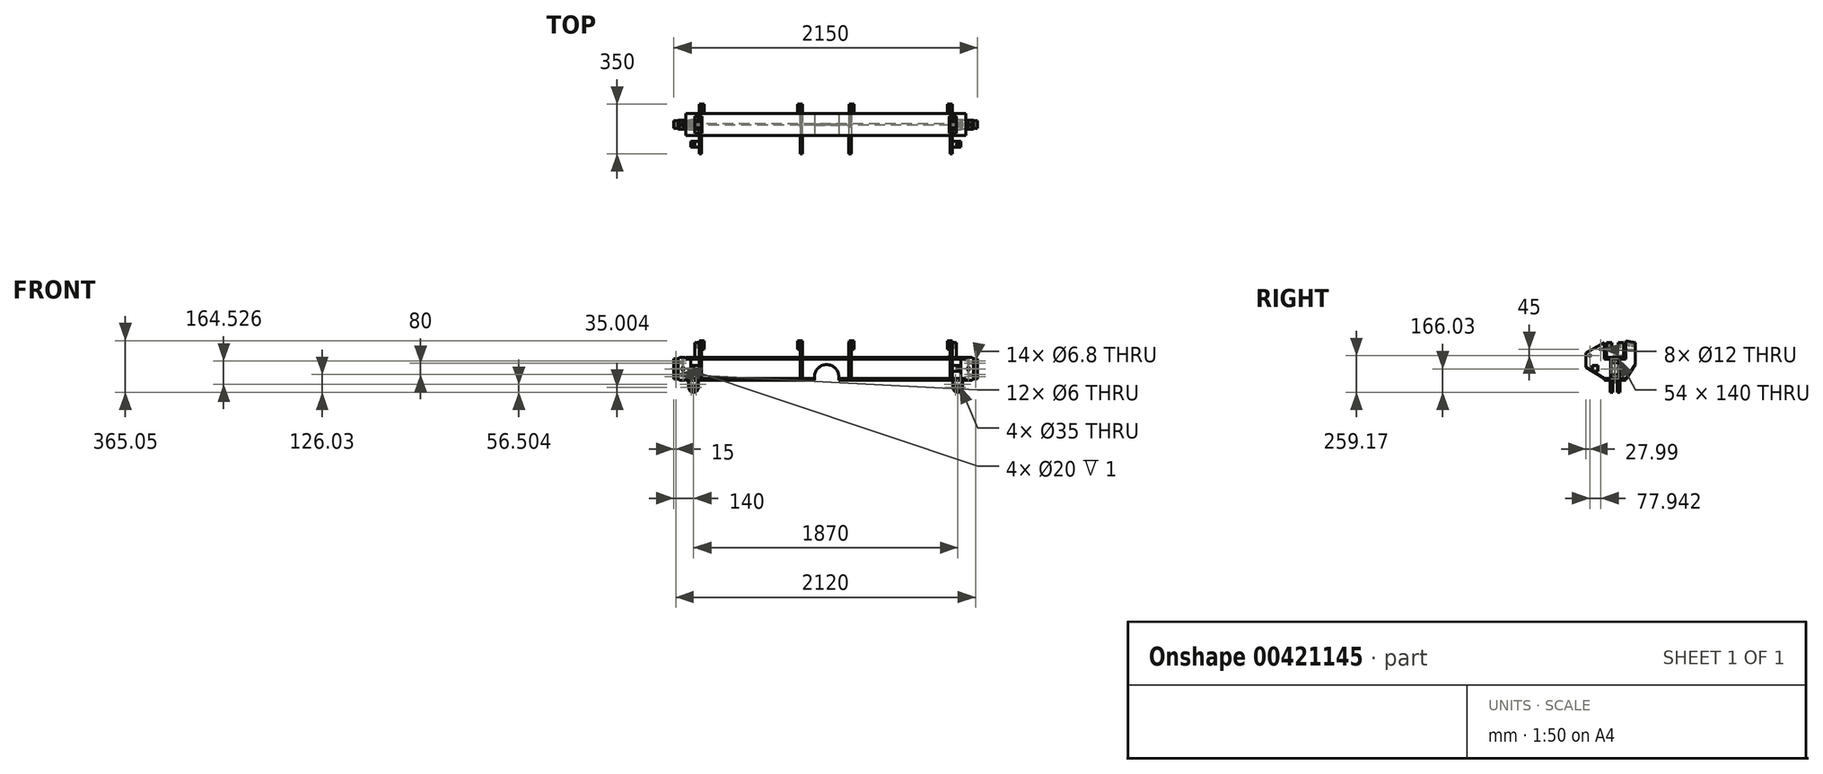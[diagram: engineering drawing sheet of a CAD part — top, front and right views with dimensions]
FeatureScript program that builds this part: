
annotation { "Feature Type Name" : "Feature", "Feature Type Description" : "" }
export const myFeature = defineFeature(function(context is Context, id is Id, definition is map)
    precondition{}
    {
        {
            var Q0;
            Q0=qCreatedBy(makeId("Right.planeOp"),FACE);
            var sketch = newSketch(context, id + "F0", { "sketchPlane" : qUnion([Q0])});
            skLineSegment(sketch, "E0.bottom", {"start": v(-77.22, 81.03) * mm, "end": v(77.22, 81.03) * mm});
            skLineSegment(sketch, "E0.top", {"start": v(-77.22, -81.03) * mm, "end": v(77.22, -81.03) * mm});
            skLineSegment(sketch, "E0.left", {"start": v(-77.22, 81.03) * mm, "end": v(-77.22, 69.47) * mm});
            skLineSegment(sketch, "E0.right", {"start": v(77.22, 81.03) * mm, "end": v(77.22, 69.47) * mm});
            skPoint(sketch, "E0.middle", {"position": v(0, 0) * mm});
            skLineSegment(sketch, "E1", {"start": v(0, 87.3) * mm, "end": v(0, -92.44) * mm, "construction": true});
            skLineSegment(sketch, "E2.0", {"start": v(-77.22, 69.47) * mm, "end": v(-16.76, 69.47) * mm});
            skLineSegment(sketch, "E3.0", {"start": v(-77.22, -69.47) * mm, "end": v(-16.76, -69.47) * mm});
            skLineSegment(sketch, "E4.0", {"start": v(-4.06, 56.77) * mm, "end": v(-4.06, -56.77) * mm});
            skLineSegment(sketch, "E5.0", {"start": v(4.06, 56.77) * mm, "end": v(4.06, -56.77) * mm});
            skLineSegment(sketch, "E6.trimOffspring", {"start": v(16.76, -69.47) * mm, "end": v(77.22, -69.47) * mm});
            skLineSegment(sketch, "E7.trimOffspring", {"start": v(16.76, 69.47) * mm, "end": v(77.22, 69.47) * mm});
            skLineSegment(sketch, "E8.trimOffspring", {"start": v(-77.22, -69.47) * mm, "end": v(-77.22, -81.03) * mm});
            skLineSegment(sketch, "E9.trimOffspring", {"start": v(77.22, -69.47) * mm, "end": v(77.22, -81.03) * mm});
            skPoint(sketch, "E10.visualSharp", {"position": v(-4.06, 69.47) * mm});
            skArc(sketch, "E10.filletArc", {"start": v(-4.06, 56.77) * mm, "mid": v(-7.78, 65.75) * mm, "end": v(-16.76, 69.47) * mm});
            skPoint(sketch, "E11.visualSharp", {"position": v(4.06, 69.47) * mm});
            skArc(sketch, "E11.filletArc", {"start": v(16.76, 69.47) * mm, "mid": v(7.78, 65.75) * mm, "end": v(4.06, 56.77) * mm});
            skPoint(sketch, "E12.visualSharp", {"position": v(4.06, -69.47) * mm});
            skArc(sketch, "E12.filletArc", {"start": v(4.06, -56.77) * mm, "mid": v(7.78, -65.75) * mm, "end": v(16.76, -69.47) * mm});
            skPoint(sketch, "E13.visualSharp", {"position": v(-4.06, -69.47) * mm});
            skArc(sketch, "E13.filletArc", {"start": v(-16.76, -69.47) * mm, "mid": v(-7.78, -65.75) * mm, "end": v(-4.06, -56.77) * mm});
            skSolve(sketch);
        }
        {
            var Q0;
            Q0=qSketchRegion(id+"F0",true);
            extrude(context, id + "F1", {"entities" : qUnion([Q0]), "endBound" : BoundingType.SYMMETRIC, "depth" : 1980 * mm});
        }
        {
            var Q0;
            Q0=makeQuery(id+"F1.opExtrude","SWEPT_FACE",FACE,{"disambiguationData":[OSD([sQuery(id+"F0.wireOp",EDGE,"E4.0")])]});
            var sketch = newSketch(context, id + "F2", { "sketchPlane" : qUnion([Q0])});
            skLineSegment(sketch, "E14", {"start": v(0, 173.84) * mm, "end": v(0, -192.2) * mm, "construction": true});
            skLineSegment(sketch, "E15.0", {"start": v(-990, 69.47) * mm, "end": v(-990, -69.47) * mm, "construction": true});
            skLineSegment(sketch, "E16.0", {"start": v(990, 69.47) * mm, "end": v(-990, 69.47) * mm, "construction": true});
            skLineSegment(sketch, "E17.0", {"start": v(990, -69.47) * mm, "end": v(-990, -69.47) * mm, "construction": true});
            skPoint(sketch, "E18.orphan", {"position": v(-990, 56.77) * mm});
            skPoint(sketch, "E19.orphan", {"position": v(-990, -56.77) * mm});
            skLineSegment(sketch, "E20.bottom", {"start": v(-990, 69.47) * mm, "end": v(-955, 69.47) * mm});
            skLineSegment(sketch, "E20.top", {"start": v(-990, -69.47) * mm, "end": v(-955, -69.47) * mm});
            skLineSegment(sketch, "E20.left", {"start": v(-990, 69.47) * mm, "end": v(-990, -69.47) * mm});
            skLineSegment(sketch, "E20.right", {"start": v(-955, 69.47) * mm, "end": v(-955, -69.47) * mm});
            skLineSegment(sketch, "E21.MirrorCS", {"start": v(990, -69.47) * mm, "end": v(955, -69.47) * mm});
            skLineSegment(sketch, "E22.MirrorCS", {"start": v(990, 69.47) * mm, "end": v(955, 69.47) * mm});
            skLineSegment(sketch, "E23.MirrorCS", {"start": v(990, 69.47) * mm, "end": v(990, -69.47) * mm});
            skLineSegment(sketch, "E24.MirrorCS", {"start": v(955, 69.47) * mm, "end": v(955, -69.47) * mm});
            skPoint(sketch, "E25.MirrorP", {"position": v(990, -56.77) * mm});
            skPoint(sketch, "E26.MirrorP", {"position": v(990, 56.77) * mm});
            skLineSegment(sketch, "E27.MirrorCS", {"start": v(990, 69.47) * mm, "end": v(990, -69.47) * mm, "construction": true});
            skSolve(sketch);
        }
        {
            var Q0;
            Q0=qSketchRegion(id+"F2",true);
            extrude(context, id + "F3", {"entities" : qUnion([Q0]), "operationType" : NewBodyOperationType.REMOVE, "endBound" : BoundingType.SYMMETRIC, "oppositeDirection" : true, "depth" : 50 * mm});
        }
        {
            var Q0;
            Q0=qCreatedBy(makeId("Front.planeOp"),FACE);
            var sketch = newSketch(context, id + "F4", { "sketchPlane" : qUnion([Q0])});
            skLineSegment(sketch, "E28", {"start": v(0, 276.7) * mm, "end": v(0, -349.05) * mm, "construction": true});
            skLineSegment(sketch, "E29.0", {"start": v(-1075, 276.7) * mm, "end": v(-1075, -349.05) * mm, "construction": true});
            skLineSegment(sketch, "E30.0", {"start": v(990, 81.03) * mm, "end": v(-1045, 81.03) * mm, "construction": true});
            skLineSegment(sketch, "E31.0", {"start": v(990, -81.03) * mm, "end": v(-1045, -81.03) * mm, "construction": true});
            skLineSegment(sketch, "E32.0", {"start": v(-955, -69.47) * mm, "end": v(-955, 69.47) * mm, "construction": true});
            skLineSegment(sketch, "E33.0", {"start": v(990, -69.47) * mm, "end": v(-990, -69.47) * mm, "construction": true});
            skLineSegment(sketch, "E34.0", {"start": v(990, 69.47) * mm, "end": v(-990, 69.47) * mm, "construction": true});
            skPoint(sketch, "E35.orphan", {"position": v(-955, 56.77) * mm});
            skPoint(sketch, "E36.orphan", {"position": v(-955, -56.77) * mm});
            skPoint(sketch, "E37.orphan", {"position": v(-990, 81.03) * mm});
            skPoint(sketch, "E38.orphan", {"position": v(-990, -81.03) * mm});
            skLineSegment(sketch, "E39", {"start": v(-990, 81.03) * mm, "end": v(-990, 69.47) * mm, "construction": true});
            skLineSegment(sketch, "E40.0", {"start": v(-1045, 81.03) * mm, "end": v(-1045, 70) * mm, "construction": true});
            skLineSegment(sketch, "E41", {"start": v(0, 0) * mm, "end": v(-1199.42, 0) * mm, "construction": true});
            skLineSegment(sketch, "E42.0", {"start": v(0, 70) * mm, "end": v(-990, 70) * mm, "construction": true});
            skLineSegment(sketch, "E43.trimOffspring", {"start": v(-1045, 70) * mm, "end": v(-1075, 70) * mm, "construction": true});
            skLineSegment(sketch, "E44.MirrorCS", {"start": v(-1045, -70) * mm, "end": v(-1075, -70) * mm, "construction": true});
            skPoint(sketch, "E45.orphan", {"position": v(-1199.42, 70) * mm});
            skPoint(sketch, "E46.orphan", {"position": v(-1199.42, -70) * mm});
            skLineSegment(sketch, "E47.trimOffspring", {"start": v(-1045, -70) * mm, "end": v(-1045, -81.03) * mm, "construction": true});
            skLineSegment(sketch, "E48.trimOffspring", {"start": v(-990, -69.47) * mm, "end": v(-990, -81.03) * mm, "construction": true});
            skLineSegment(sketch, "E49.bottom", {"start": v(-1075, 70) * mm, "end": v(-1045, 70) * mm});
            skLineSegment(sketch, "E49.top", {"start": v(-1075, -70) * mm, "end": v(-1045, -70) * mm});
            skLineSegment(sketch, "E49.left", {"start": v(-1075, 70) * mm, "end": v(-1075, -70) * mm});
            skLineSegment(sketch, "E50.bottom", {"start": v(-1045, 81.03) * mm, "end": v(-990, 81.03) * mm});
            skLineSegment(sketch, "E50.top", {"start": v(-1045, -81.03) * mm, "end": v(-990, -81.03) * mm});
            skLineSegment(sketch, "E50.left", {"start": v(-1045, 81.03) * mm, "end": v(-1045, 70) * mm});
            skLineSegment(sketch, "E50.right", {"start": v(-990, 81.03) * mm, "end": v(-990, 69.47) * mm});
            skLineSegment(sketch, "E51.bottom", {"start": v(-990, 70) * mm, "end": v(-955, 70) * mm});
            skLineSegment(sketch, "E51.top", {"start": v(-990, -69.47) * mm, "end": v(-955, -69.47) * mm});
            skLineSegment(sketch, "E51.left", {"start": v(-990, 70) * mm, "end": v(-990, 69.47) * mm});
            skLineSegment(sketch, "E51.right", {"start": v(-955, 70) * mm, "end": v(-955, -69.47) * mm});
            skLineSegment(sketch, "E52.trimOffspring", {"start": v(-990, -69.47) * mm, "end": v(-990, -81.03) * mm});
            skLineSegment(sketch, "E53.trimOffspring", {"start": v(-1045, -70) * mm, "end": v(-1045, -81.03) * mm});
            skSolve(sketch);
        }
        {
            var Q0;
            Q0=qSketchRegion(id+"F4",true);
            extrude(context, id + "F5", {"entities" : qUnion([Q0]), "endBound" : BoundingType.SYMMETRIC, "depth" : 63.5 * mm});
        }
        {
            var Q0;
            Q0=makeQuery(id+"F5.opExtrude","SWEPT_FACE",FACE,{"disambiguationData":[OSD([sQuery(id+"F4.wireOp",EDGE,"E49.bottom")])]});
            var sketch = newSketch(context, id + "F6", { "sketchPlane" : qUnion([Q0])});
            skLineSegment(sketch, "E54", {"start": v(-948.4, 0) * mm, "end": v(-1101.52, 0) * mm, "construction": true});
            skLineSegment(sketch, "E55.0", {"start": v(-1045, -31.75) * mm, "end": v(-1045, 31.75) * mm, "construction": true});
            skLineSegment(sketch, "E56.0", {"start": v(-948.4, 27) * mm, "end": v(-1101.52, 27) * mm, "construction": true});
            skLineSegment(sketch, "E57.bottom", {"start": v(-1075, 31.75) * mm, "end": v(-1045, 31.75) * mm});
            skLineSegment(sketch, "E57.top", {"start": v(-1075, 27) * mm, "end": v(-1045, 27) * mm});
            skLineSegment(sketch, "E57.left", {"start": v(-1075, 31.75) * mm, "end": v(-1075, 27) * mm});
            skLineSegment(sketch, "E57.right", {"start": v(-1045, 31.75) * mm, "end": v(-1045, 27) * mm});
            skLineSegment(sketch, "E58.MirrorCS", {"start": v(-1045, -31.75) * mm, "end": v(-1045, -27) * mm});
            skLineSegment(sketch, "E59.MirrorCS", {"start": v(-1075, -31.75) * mm, "end": v(-1075, -27) * mm});
            skLineSegment(sketch, "E60.MirrorCS", {"start": v(-1075, -27) * mm, "end": v(-1045, -27) * mm});
            skLineSegment(sketch, "E61.MirrorCS", {"start": v(-1075, -31.75) * mm, "end": v(-1045, -31.75) * mm});
            skSolve(sketch);
        }
        {
            var Q0;
            Q0=qSketchRegion(id+"F6",true);
            extrude(context, id + "F7", {"entities" : qUnion([Q0]), "operationType" : NewBodyOperationType.REMOVE, "endBound" : BoundingType.THROUGH_ALL, "oppositeDirection" : true, "depth" : 25 * mm});
        }
        {
            var Q0;
            Q0=makeQuery(id+"F5.opExtrude","SWEPT_FACE",FACE,{"disambiguationData":[OSD([sQuery(id+"F4.wireOp",EDGE,"E50.bottom")])]});
            var sketch = newSketch(context, id + "F8", { "sketchPlane" : qUnion([Q0])});
            skLineSegment(sketch, "E62.0", {"start": v(-1075, -27) * mm, "end": v(-1075, 27) * mm, "construction": true});
            skLineSegment(sketch, "E63", {"start": v(-919.6, 0) * mm, "end": v(-1088.25, 0) * mm, "construction": true});
            skPoint(sketch, "E63.endSnap0", {"position": v(-1075, 0) * mm});
            skLineSegment(sketch, "E64.0", {"start": v(-1010, -27) * mm, "end": v(-1010, 27) * mm, "construction": true});
            skPoint(sketch, "E65", {"position": v(-1010, 0) * mm});
            skSolve(sketch);
        }
        {
            var Q0;
            Q0=sQuery(id+"F8.wireOp",VERTEX,"E65");
            var Q1;
            Q1=makeQuery(id+"F5.opExtrude","SWEPT_BODY",BODY,{"disambiguationData":[OSD([sQuery(id+"F4.wireOp",EDGE,"E49.bottom"),sQuery(id+"F4.wireOp",EDGE,"E49.top"),sQuery(id+"F4.wireOp",EDGE,"E49.left"),sQuery(id+"F4.wireOp",EDGE,"E50.bottom"),sQuery(id+"F4.wireOp",EDGE,"E50.top"),sQuery(id+"F4.wireOp",EDGE,"E50.left"),sQuery(id+"F4.wireOp",EDGE,"E50.right"),sQuery(id+"F4.wireOp",EDGE,"E51.bottom"),sQuery(id+"F4.wireOp",EDGE,"E51.top"),sQuery(id+"F4.wireOp",EDGE,"E51.right"),sQuery(id+"F4.wireOp",EDGE,"E52.trimOffspring"),sQuery(id+"F4.wireOp",EDGE,"E53.trimOffspring")])]});
            hole(context, id + "F9", {"style" : HoleStyle.SIMPLE, "endStyle" : HoleEndStyle.BLIND, "standardTappedOrClearance" : lookupTablePath({ "standard" : "ISO", "size" : "6", "type" : "Drilled" }), "standardBlindInLast" : lookupTablePath({ "standard" : "ISO", "size" : "6", "type" : "Drilled" }), "holeDiameter" : 6 * mm, "holeDepth" : 125 * mm, "locations" : qUnion([Q0]), "scope" : qUnion([Q1])});
        }
        {
            var Q0;
            Q0=sQuery(id+"F8.wireOp",VERTEX,"E65");
            var Q1;
            Q1=makeQuery(id+"F5.opExtrude","SWEPT_BODY",BODY,{"disambiguationData":[OSD([sQuery(id+"F4.wireOp",EDGE,"E49.bottom"),sQuery(id+"F4.wireOp",EDGE,"E49.top"),sQuery(id+"F4.wireOp",EDGE,"E49.left"),sQuery(id+"F4.wireOp",EDGE,"E50.bottom"),sQuery(id+"F4.wireOp",EDGE,"E50.top"),sQuery(id+"F4.wireOp",EDGE,"E50.left"),sQuery(id+"F4.wireOp",EDGE,"E50.right"),sQuery(id+"F4.wireOp",EDGE,"E51.bottom"),sQuery(id+"F4.wireOp",EDGE,"E51.top"),sQuery(id+"F4.wireOp",EDGE,"E51.right"),sQuery(id+"F4.wireOp",EDGE,"E52.trimOffspring"),sQuery(id+"F4.wireOp",EDGE,"E53.trimOffspring")])]});
            hole(context, id + "F10", {"style" : HoleStyle.SIMPLE, "endStyle" : HoleEndStyle.BLIND, "standardTappedOrClearance" : lookupTablePath({ "standard" : "ANSI", "engagement" : "75%", "pitch" : "13 tpi", "size" : "1/2", "type" : "Tapped" }), "standardBlindInLast" : lookupTablePath({ "standard" : "ANSI", "engagement" : "75%", "pitch" : "13 tpi", "size" : "1/2", "type" : "Tapped" }), "holeDiameter" : 10.72 * mm, "holeDepth" : 15 * mm, "locations" : qUnion([Q0]), "scope" : qUnion([Q1]), "majorDiameter" : 12.7 * mm});
        }
        {
            var Q0;
            {var subQ0=sQuery(id+"F4.wireOp",EDGE,"E50.bottom");Q0=makeQuery(id+"F8.imprint","IMPRINT",FACE,{"disambiguationData":[TD([[makeQuery(id+"F8.imprint","IMPRINT",EDGE,{"derivedFrom":makeQuery(id+"F5.opExtrude","CAP_EDGE",EDGE,{"disambiguationData":[OSD([subQ0])],"isStart":true})}),-1.0]])]});}
            var sketch = newSketch(context, id + "F11", { "sketchPlane" : qUnion([Q0])});
            skPoint(sketch, "E66.0", {"position": v(-1010, 0) * mm});
            skCircle(sketch, "E67", {"center": v(-1010, 0) * mm, "radius": 10 * mm});
            skSolve(sketch);
        }
        {
            var Q0;
            Q0=qSketchRegion(id+"F11",true);
            extrude(context, id + "F12", {"entities" : qUnion([Q0]), "operationType" : NewBodyOperationType.REMOVE, "oppositeDirection" : true, "depth" : 1 * mm});
        }
        {
            var Q0;
            Q0=makeQuery(id+"F5.opExtrude","SWEPT_EDGE",EDGE,{"disambiguationData":[OSD([sQuery(id+"F4.wireOp",EDGE,"E50.bottom"),sQuery(id+"F4.wireOp",EDGE,"E50.left")])]});
            var Q1;
            Q1=makeQuery(id+"F7.boolean.opBoolean","INTERSECT",EDGE,{"derivedFrom":[makeQuery(id+"F7.opExtrude","SWEPT_FACE",FACE,{"disambiguationData":[OSD([sQuery(id+"F6.wireOp",EDGE,"E57.right")])]}),makeQuery(id+"F7.opExtrude","SWEPT_FACE",FACE,{"disambiguationData":[OSD([sQuery(id+"F6.wireOp",EDGE,"E58.MirrorCS")])]})]});
            chamfer(context, id + "F13", {"entities" : qUnion([Q0, Q1]), "width" : 11 * mm, "tangentPropagation" : true});
        }
        {
            var Q0;
            Q0=makeQuery(id+"F5.opExtrude","CAP_FACE",FACE,{"disambiguationData":[OSD([sQuery(id+"F4.wireOp",EDGE,"E49.bottom"),sQuery(id+"F4.wireOp",EDGE,"E49.top"),sQuery(id+"F4.wireOp",EDGE,"E49.left"),sQuery(id+"F4.wireOp",EDGE,"E50.bottom"),sQuery(id+"F4.wireOp",EDGE,"E50.top"),sQuery(id+"F4.wireOp",EDGE,"E50.left"),sQuery(id+"F4.wireOp",EDGE,"E50.right"),sQuery(id+"F4.wireOp",EDGE,"E51.bottom"),sQuery(id+"F4.wireOp",EDGE,"E51.top"),sQuery(id+"F4.wireOp",EDGE,"E51.right"),sQuery(id+"F4.wireOp",EDGE,"E52.trimOffspring"),sQuery(id+"F4.wireOp",EDGE,"E53.trimOffspring")])],"isStart":false});
            var sketch = newSketch(context, id + "F14", { "sketchPlane" : qUnion([Q0])});
            skLineSegment(sketch, "E68", {"start": v(-947.26, 0.27) * mm, "end": v(-1104.17, 0.27) * mm, "construction": true});
            skPoint(sketch, "E68.startSnap0", {"position": v(-955, 0.27) * mm});
            skLineSegment(sketch, "E69.0", {"start": v(-1075, -70) * mm, "end": v(-1075, 70) * mm, "construction": true});
            skLineSegment(sketch, "E70.0", {"start": v(-1010, -70) * mm, "end": v(-1010, 70) * mm, "construction": true});
            skPoint(sketch, "E71", {"position": v(-1010, 0.27) * mm});
            skSolve(sketch);
        }
        {
            var Q0;
            Q0=sQuery(id+"F14.wireOp",VERTEX,"E71");
            var Q1;
            Q1=makeQuery(id+"F5.opExtrude","SWEPT_BODY",BODY,{"disambiguationData":[OSD([sQuery(id+"F4.wireOp",EDGE,"E49.bottom"),sQuery(id+"F4.wireOp",EDGE,"E49.top"),sQuery(id+"F4.wireOp",EDGE,"E49.left"),sQuery(id+"F4.wireOp",EDGE,"E50.bottom"),sQuery(id+"F4.wireOp",EDGE,"E50.top"),sQuery(id+"F4.wireOp",EDGE,"E50.left"),sQuery(id+"F4.wireOp",EDGE,"E50.right"),sQuery(id+"F4.wireOp",EDGE,"E51.bottom"),sQuery(id+"F4.wireOp",EDGE,"E51.top"),sQuery(id+"F4.wireOp",EDGE,"E51.right"),sQuery(id+"F4.wireOp",EDGE,"E52.trimOffspring"),sQuery(id+"F4.wireOp",EDGE,"E53.trimOffspring")])]});
            hole(context, id + "F15", {"style" : HoleStyle.SIMPLE, "endStyle" : HoleEndStyle.BLIND, "standardTappedOrClearance" : lookupTablePath({ "standard" : "ANSI", "engagement" : "75%", "pitch" : "13 tpi", "size" : "1/2", "type" : "Tapped" }), "standardBlindInLast" : lookupTablePath({ "standard" : "ANSI", "engagement" : "75%", "pitch" : "13 tpi", "size" : "1/2", "type" : "Tapped" }), "holeDiameter" : 10.72 * mm, "holeDepth" : 15 * mm, "locations" : qUnion([Q0]), "scope" : qUnion([Q1]), "majorDiameter" : 12.7 * mm});
        }
        {
            var Q0;
            Q0=sQuery(id+"F14.wireOp",VERTEX,"E71");
            var Q1;
            Q1=makeQuery(id+"F5.opExtrude","SWEPT_BODY",BODY,{"disambiguationData":[OSD([sQuery(id+"F4.wireOp",EDGE,"E49.bottom"),sQuery(id+"F4.wireOp",EDGE,"E49.top"),sQuery(id+"F4.wireOp",EDGE,"E49.left"),sQuery(id+"F4.wireOp",EDGE,"E50.bottom"),sQuery(id+"F4.wireOp",EDGE,"E50.top"),sQuery(id+"F4.wireOp",EDGE,"E50.left"),sQuery(id+"F4.wireOp",EDGE,"E50.right"),sQuery(id+"F4.wireOp",EDGE,"E51.bottom"),sQuery(id+"F4.wireOp",EDGE,"E51.top"),sQuery(id+"F4.wireOp",EDGE,"E51.right"),sQuery(id+"F4.wireOp",EDGE,"E52.trimOffspring"),sQuery(id+"F4.wireOp",EDGE,"E53.trimOffspring")])]});
            hole(context, id + "F16", {"style" : HoleStyle.SIMPLE, "endStyle" : HoleEndStyle.THROUGH, "standardTappedOrClearance" : lookupTablePath({ "standard" : "ISO", "size" : "6", "type" : "Drilled" }), "standardBlindInLast" : lookupTablePath({ "standard" : "ISO", "size" : "6", "type" : "Drilled" }), "holeDiameter" : 6 * mm, "locations" : qUnion([Q0]), "scope" : qUnion([Q1]), "isTappedThrough" : true});
        }
        {
            var Q0;
            {var subQ4=sQuery(id+"F4.wireOp",EDGE,"E50.right");Q0=makeQuery(id+"F14.imprint","IMPRINT",FACE,{"disambiguationData":[TD([[makeQuery(id+"F14.imprint","IMPRINT",EDGE,{"derivedFrom":makeQuery(id+"F5.opExtrude","CAP_EDGE",EDGE,{"disambiguationData":[OSD([subQ4])],"isStart":false})}),-1.0]])]});}
            var sketch = newSketch(context, id + "F17", { "sketchPlane" : qUnion([Q0])});
            skCircle(sketch, "E72", {"center": v(-1010, 0.27) * mm, "radius": 10 * mm});
            skSolve(sketch);
        }
        {
            var Q0;
            Q0=qSketchRegion(id+"F17",true);
            extrude(context, id + "F18", {"entities" : qUnion([Q0]), "operationType" : NewBodyOperationType.REMOVE, "oppositeDirection" : true, "depth" : 1 * mm});
        }
        {
            var Q0;
            Q0=makeQuery(id+"F5.opExtrude","CAP_FACE",FACE,{"disambiguationData":[OSD([sQuery(id+"F4.wireOp",EDGE,"E49.bottom"),sQuery(id+"F4.wireOp",EDGE,"E49.top"),sQuery(id+"F4.wireOp",EDGE,"E49.left"),sQuery(id+"F4.wireOp",EDGE,"E50.bottom"),sQuery(id+"F4.wireOp",EDGE,"E50.top"),sQuery(id+"F4.wireOp",EDGE,"E50.left"),sQuery(id+"F4.wireOp",EDGE,"E50.right"),sQuery(id+"F4.wireOp",EDGE,"E51.bottom"),sQuery(id+"F4.wireOp",EDGE,"E51.top"),sQuery(id+"F4.wireOp",EDGE,"E51.right"),sQuery(id+"F4.wireOp",EDGE,"E52.trimOffspring"),sQuery(id+"F4.wireOp",EDGE,"E53.trimOffspring")])],"isStart":true});
            var sketch = newSketch(context, id + "F19", { "sketchPlane" : qUnion([Q0])});
            skCircle(sketch, "E73.0", {"center": v(1010, 0.27) * mm, "radius": 10 * mm, "construction": true});
            skCircle(sketch, "E74", {"center": v(1010, 0.27) * mm, "radius": 10 * mm});
            skSolve(sketch);
        }
        {
            var Q0;
            Q0=qSketchRegion(id+"F19",true);
            extrude(context, id + "F20", {"entities" : qUnion([Q0]), "operationType" : NewBodyOperationType.REMOVE, "oppositeDirection" : true, "depth" : 1 * mm});
        }
        {
            var Q0;
            Q0=sQuery(id+"F19.wireOp",VERTEX,"E73.0.center");
            var Q1;
            Q1=makeQuery(id+"F5.opExtrude","SWEPT_BODY",BODY,{"disambiguationData":[OSD([sQuery(id+"F4.wireOp",EDGE,"E49.bottom"),sQuery(id+"F4.wireOp",EDGE,"E49.top"),sQuery(id+"F4.wireOp",EDGE,"E49.left"),sQuery(id+"F4.wireOp",EDGE,"E50.bottom"),sQuery(id+"F4.wireOp",EDGE,"E50.top"),sQuery(id+"F4.wireOp",EDGE,"E50.left"),sQuery(id+"F4.wireOp",EDGE,"E50.right"),sQuery(id+"F4.wireOp",EDGE,"E51.bottom"),sQuery(id+"F4.wireOp",EDGE,"E51.top"),sQuery(id+"F4.wireOp",EDGE,"E51.right"),sQuery(id+"F4.wireOp",EDGE,"E52.trimOffspring"),sQuery(id+"F4.wireOp",EDGE,"E53.trimOffspring")])]});
            hole(context, id + "F21", {"style" : HoleStyle.SIMPLE, "endStyle" : HoleEndStyle.BLIND, "standardTappedOrClearance" : lookupTablePath({ "standard" : "ANSI", "engagement" : "75%", "pitch" : "13 tpi", "size" : "1/2", "type" : "Tapped" }), "standardBlindInLast" : lookupTablePath({ "standard" : "ANSI", "engagement" : "75%", "pitch" : "13 tpi", "size" : "1/2", "type" : "Tapped" }), "holeDiameter" : 10.72 * mm, "holeDepth" : 15 * mm, "locations" : qUnion([Q0]), "scope" : qUnion([Q1]), "majorDiameter" : 12.7 * mm});
        }
        {
            var Q0;
            Q0=makeQuery(id+"F7.boolean.opBoolean","COPY",FACE,{"derivedFrom":makeQuery(id+"F7.opExtrude","SWEPT_FACE",FACE,{"disambiguationData":[OSD([sQuery(id+"F6.wireOp",EDGE,"E60.MirrorCS")])]})});
            var sketch = newSketch(context, id + "F22", { "sketchPlane" : qUnion([Q0])});
            skLineSegment(sketch, "E75.0", {"start": v(-1075, -70) * mm, "end": v(-1075, 70) * mm, "construction": true});
            skLineSegment(sketch, "E76.0", {"start": v(-1060, -70) * mm, "end": v(-1060, 70) * mm, "construction": true});
            skLineSegment(sketch, "E77", {"start": v(-1060, 0) * mm, "end": v(-1136.9, 0) * mm, "construction": true});
            skLineSegment(sketch, "E78.0", {"start": v(-1060, 55) * mm, "end": v(-1136.9, 55) * mm, "construction": true});
            skLineSegment(sketch, "E79.0", {"start": v(-1060, -55) * mm, "end": v(-1136.9, -55) * mm, "construction": true});
            skPoint(sketch, "E80", {"position": v(-1060, 55) * mm});
            skPoint(sketch, "E81", {"position": v(-1060, 0) * mm});
            skPoint(sketch, "E82", {"position": v(-1060, -55) * mm});
            skSolve(sketch);
        }
        {
            var Q0;
            Q0=sQuery(id+"F22.wireOp",VERTEX,"E80");
            var Q1;
            Q1=sQuery(id+"F22.wireOp",VERTEX,"E81");
            var Q2;
            Q2=sQuery(id+"F22.wireOp",VERTEX,"E82");
            var Q3;
            Q3=makeQuery(id+"F5.opExtrude","SWEPT_BODY",BODY,{"disambiguationData":[OSD([sQuery(id+"F4.wireOp",EDGE,"E49.bottom"),sQuery(id+"F4.wireOp",EDGE,"E49.top"),sQuery(id+"F4.wireOp",EDGE,"E49.left"),sQuery(id+"F4.wireOp",EDGE,"E50.bottom"),sQuery(id+"F4.wireOp",EDGE,"E50.top"),sQuery(id+"F4.wireOp",EDGE,"E50.left"),sQuery(id+"F4.wireOp",EDGE,"E50.right"),sQuery(id+"F4.wireOp",EDGE,"E51.bottom"),sQuery(id+"F4.wireOp",EDGE,"E51.top"),sQuery(id+"F4.wireOp",EDGE,"E51.right"),sQuery(id+"F4.wireOp",EDGE,"E52.trimOffspring"),sQuery(id+"F4.wireOp",EDGE,"E53.trimOffspring")])]});
            hole(context, id + "F23", {"style" : HoleStyle.SIMPLE, "endStyle" : HoleEndStyle.THROUGH, "standardTappedOrClearance" : lookupTablePath({ "standard" : "ISO", "engagement" : "75%", "pitch" : "1.25 mm", "size" : "M8", "type" : "Tapped" }), "standardBlindInLast" : lookupTablePath({ "standard" : "ISO", "engagement" : "75%", "pitch" : "1.25 mm", "size" : "M8", "type" : "Tapped" }), "holeDiameter" : 6.8 * mm, "locations" : qUnion([Q0, Q1, Q2]), "scope" : qUnion([Q3]), "isTappedThrough" : true, "majorDiameter" : 8 * mm, "showTappedDepth" : true});
        }
        {
            var Q0;
            Q0=makeQuery(id+"F7.boolean.opBoolean","COPY",FACE,{"derivedFrom":makeQuery(id+"F7.opExtrude","SWEPT_FACE",FACE,{"disambiguationData":[OSD([sQuery(id+"F6.wireOp",EDGE,"E60.MirrorCS")])]})});
            var sketch = newSketch(context, id + "F24", { "sketchPlane" : qUnion([Q0])});
            skLineSegment(sketch, "E83.0", {"start": v(-1060, 0) * mm, "end": v(-1136.9, 0) * mm, "construction": true});
            skLineSegment(sketch, "E84.0", {"start": v(-1060, -70) * mm, "end": v(-1060, 70) * mm, "construction": true});
            skLineSegment(sketch, "E85.0", {"start": v(-1060, 40) * mm, "end": v(-1136.9, 40) * mm, "construction": true});
            skPoint(sketch, "E86", {"position": v(-1060, 40) * mm});
            skPoint(sketch, "E87.MirrorP", {"position": v(-1060, -40) * mm});
            skSolve(sketch);
        }
        {
            var Q0;
            Q0=sQuery(id+"F24.wireOp",VERTEX,"E86");
            var Q1;
            Q1=sQuery(id+"F24.wireOp",VERTEX,"E87.MirrorP");
            var Q2;
            Q2=makeQuery(id+"F5.opExtrude","SWEPT_BODY",BODY,{"disambiguationData":[OSD([sQuery(id+"F4.wireOp",EDGE,"E49.bottom"),sQuery(id+"F4.wireOp",EDGE,"E49.top"),sQuery(id+"F4.wireOp",EDGE,"E49.left"),sQuery(id+"F4.wireOp",EDGE,"E50.bottom"),sQuery(id+"F4.wireOp",EDGE,"E50.top"),sQuery(id+"F4.wireOp",EDGE,"E50.left"),sQuery(id+"F4.wireOp",EDGE,"E50.right"),sQuery(id+"F4.wireOp",EDGE,"E51.bottom"),sQuery(id+"F4.wireOp",EDGE,"E51.top"),sQuery(id+"F4.wireOp",EDGE,"E51.right"),sQuery(id+"F4.wireOp",EDGE,"E52.trimOffspring"),sQuery(id+"F4.wireOp",EDGE,"E53.trimOffspring")])]});
            hole(context, id + "F25", {"style" : HoleStyle.SIMPLE, "endStyle" : HoleEndStyle.THROUGH, "standardTappedOrClearance" : lookupTablePath({ "standard" : "ISO", "size" : "6", "type" : "Drilled" }), "standardBlindInLast" : lookupTablePath({ "standard" : "ISO", "size" : "6", "type" : "Drilled" }), "holeDiameter" : 6 * mm, "locations" : qUnion([Q0, Q1]), "scope" : qUnion([Q2]), "isTappedThrough" : true});
        }
        {
            var Q0;
            Q0=makeQuery(id+"F5.opExtrude","SWEPT_FACE",FACE,{"disambiguationData":[OSD([sQuery(id+"F4.wireOp",EDGE,"E49.left")])]});
            var sketch = newSketch(context, id + "F26", { "sketchPlane" : qUnion([Q0])});
            skLineSegment(sketch, "E88.0.0", {"start": v(-27, -70) * mm, "end": v(27, -70) * mm, "construction": true});
            skLineSegment(sketch, "E88.0.1", {"start": v(27, -70) * mm, "end": v(27, 70) * mm, "construction": true});
            skLineSegment(sketch, "E88.0.2", {"start": v(27, 70) * mm, "end": v(-27, 70) * mm, "construction": true});
            skLineSegment(sketch, "E88.0.3", {"start": v(-27, 70) * mm, "end": v(-27, -70) * mm, "construction": true});
            skLineSegment(sketch, "E89", {"start": v(-27, 0) * mm, "end": v(56.48, 0) * mm, "construction": true});
            skPoint(sketch, "E89.endSnap0", {"position": v(-27, 0) * mm});
            skLineSegment(sketch, "E90", {"start": v(0, 96.87) * mm, "end": v(0, -94.28) * mm, "construction": true});
            skLineSegment(sketch, "E91.0", {"start": v(-27, -40) * mm, "end": v(56.48, -40) * mm, "construction": true});
            skPoint(sketch, "E92", {"position": v(0, -40) * mm});
            skPoint(sketch, "E93.MirrorP", {"position": v(0, 40) * mm});
            skSolve(sketch);
        }
        {
            var Q0;
            Q0=sQuery(id+"F26.wireOp",VERTEX,"E93.MirrorP");
            var Q1;
            Q1=sQuery(id+"F26.wireOp",VERTEX,"E92");
            var Q2;
            Q2=makeQuery(id+"F5.opExtrude","SWEPT_BODY",BODY,{"disambiguationData":[OSD([sQuery(id+"F4.wireOp",EDGE,"E49.bottom"),sQuery(id+"F4.wireOp",EDGE,"E49.top"),sQuery(id+"F4.wireOp",EDGE,"E49.left"),sQuery(id+"F4.wireOp",EDGE,"E50.bottom"),sQuery(id+"F4.wireOp",EDGE,"E50.top"),sQuery(id+"F4.wireOp",EDGE,"E50.left"),sQuery(id+"F4.wireOp",EDGE,"E50.right"),sQuery(id+"F4.wireOp",EDGE,"E51.bottom"),sQuery(id+"F4.wireOp",EDGE,"E51.top"),sQuery(id+"F4.wireOp",EDGE,"E51.right"),sQuery(id+"F4.wireOp",EDGE,"E52.trimOffspring"),sQuery(id+"F4.wireOp",EDGE,"E53.trimOffspring")])]});
            hole(context, id + "F27", {"style" : HoleStyle.SIMPLE, "endStyle" : HoleEndStyle.BLIND, "standardTappedOrClearance" : lookupTablePath({ "standard" : "ISO", "size" : "6", "type" : "Drilled" }), "standardBlindInLast" : lookupTablePath({ "standard" : "ISO", "size" : "6", "type" : "Drilled" }), "holeDiameter" : 6 * mm, "holeDepth" : 65 * mm, "locations" : qUnion([Q0, Q1]), "scope" : qUnion([Q2])});
        }
        {
            var Q0;
            Q0=sQuery(id+"F26.wireOp",VERTEX,"E93.MirrorP");
            var Q1;
            Q1=sQuery(id+"F26.wireOp",VERTEX,"E92");
            var Q2;
            Q2=makeQuery(id+"F5.opExtrude","SWEPT_BODY",BODY,{"disambiguationData":[OSD([sQuery(id+"F4.wireOp",EDGE,"E49.bottom"),sQuery(id+"F4.wireOp",EDGE,"E49.top"),sQuery(id+"F4.wireOp",EDGE,"E49.left"),sQuery(id+"F4.wireOp",EDGE,"E50.bottom"),sQuery(id+"F4.wireOp",EDGE,"E50.top"),sQuery(id+"F4.wireOp",EDGE,"E50.left"),sQuery(id+"F4.wireOp",EDGE,"E50.right"),sQuery(id+"F4.wireOp",EDGE,"E51.bottom"),sQuery(id+"F4.wireOp",EDGE,"E51.top"),sQuery(id+"F4.wireOp",EDGE,"E51.right"),sQuery(id+"F4.wireOp",EDGE,"E52.trimOffspring"),sQuery(id+"F4.wireOp",EDGE,"E53.trimOffspring")])]});
            hole(context, id + "F28", {"style" : HoleStyle.SIMPLE, "endStyle" : HoleEndStyle.BLIND, "standardTappedOrClearance" : lookupTablePath({ "standard" : "ISO", "engagement" : "75%", "pitch" : "1.25 mm", "size" : "M8", "type" : "Tapped" }), "standardBlindInLast" : lookupTablePath({ "standard" : "ISO", "engagement" : "75%", "pitch" : "1.25 mm", "size" : "M8", "type" : "Tapped" }), "holeDiameter" : 6.8 * mm, "holeDepth" : 12 * mm, "locations" : qUnion([Q0, Q1]), "scope" : qUnion([Q2]), "majorDiameter" : 8 * mm});
        }
        {
            var Q0;
            Q0=makeQuery(id+"F5.opExtrude","SWEPT_BODY",BODY,{"disambiguationData":[OSD([sQuery(id+"F4.wireOp",EDGE,"E49.bottom"),sQuery(id+"F4.wireOp",EDGE,"E49.top"),sQuery(id+"F4.wireOp",EDGE,"E49.left"),sQuery(id+"F4.wireOp",EDGE,"E50.bottom"),sQuery(id+"F4.wireOp",EDGE,"E50.top"),sQuery(id+"F4.wireOp",EDGE,"E50.left"),sQuery(id+"F4.wireOp",EDGE,"E50.right"),sQuery(id+"F4.wireOp",EDGE,"E51.bottom"),sQuery(id+"F4.wireOp",EDGE,"E51.top"),sQuery(id+"F4.wireOp",EDGE,"E51.right"),sQuery(id+"F4.wireOp",EDGE,"E52.trimOffspring"),sQuery(id+"F4.wireOp",EDGE,"E53.trimOffspring")])]});
            var Q1;
            Q1=qCreatedBy(makeId("Right.planeOp"),FACE);
            mirror(context, id + "F29", {"entities" : qUnion([Q0]), "mirrorPlane" : qUnion([Q1])});
        }
        {
            var Q0;
            Q0=qCreatedBy(makeId("Front.planeOp"),FACE);
            var sketch = newSketch(context, id + "F30", { "sketchPlane" : qUnion([Q0])});
            skLineSegment(sketch, "E94", {"start": v(0, 217.37) * mm, "end": v(0, -483.51) * mm, "construction": true});
            skLineSegment(sketch, "E95.0", {"start": v(-935, 217.37) * mm, "end": v(-935, -483.51) * mm, "construction": true});
            skLineSegment(sketch, "E96.0.0", {"start": v(-990, -69.47) * mm, "end": v(-990, -81.03) * mm, "construction": true});
            skLineSegment(sketch, "E96.0.1", {"start": v(-990, -81.03) * mm, "end": v(-900, -81.03) * mm});
            skLineSegment(sketch, "E96.0.2", {"start": v(990, -81.03) * mm, "end": v(990, -69.47) * mm, "construction": true});
            skLineSegment(sketch, "E96.0.3", {"start": v(990, -69.47) * mm, "end": v(-990, -69.47) * mm, "construction": true});
            skLineSegment(sketch, "E97.0", {"start": v(-990, -131.03) * mm, "end": v(990, -131.03) * mm, "construction": true});
            skCircle(sketch, "E98", {"center": v(-935, -131.03) * mm, "radius": 17.5 * mm});
            skArc(sketch, "E99", {"start": v(-970, -131.03) * mm, "mid": v(-935, -166.03) * mm, "end": v(-900, -131.03) * mm});
            skLineSegment(sketch, "E100", {"start": v(-970, -131.03) * mm, "end": v(-970, -81.03) * mm});
            skLineSegment(sketch, "E101", {"start": v(-900, -131.03) * mm, "end": v(-900, -81.03) * mm});
            skLineSegment(sketch, "E102.trimOffspring", {"start": v(0, -81.03) * mm, "end": v(990, -81.03) * mm});
            skLineSegment(sketch, "E103", {"start": v(-935, -166.03) * mm, "end": v(-989.6, -166.03) * mm, "construction": true});
            skLineSegment(sketch, "E104.0", {"start": v(-935, -144.53) * mm, "end": v(-989.6, -144.53) * mm, "construction": true});
            skLineSegment(sketch, "E105.0", {"start": v(-990, -109.53) * mm, "end": v(990, -109.53) * mm, "construction": true});
            skLineSegment(sketch, "E106.0", {"start": v(-953, 217.37) * mm, "end": v(-953, -483.51) * mm, "construction": true});
            skPoint(sketch, "E107", {"position": v(-953, -109.53) * mm});
            skPoint(sketch, "E108.MirrorP", {"position": v(-917, -109.53) * mm});
            skSolve(sketch);
        }
        {
            var Q0;
            Q0=qSketchRegion(id+"F30",true);
            extrude(context, id + "F31", {"entities" : qUnion([Q0]), "endBound" : BoundingType.SYMMETRIC, "depth" : 70 * mm});
        }
        {
            var Q0;
            Q0=makeQuery(id+"F31.opExtrude","CAP_FACE",FACE,{"disambiguationData":[OSD([sQuery(id+"F30.wireOp",EDGE,"E96.0.1"),sQuery(id+"F30.wireOp",EDGE,"E98"),sQuery(id+"F30.wireOp",EDGE,"E99"),sQuery(id+"F30.wireOp",EDGE,"E100"),sQuery(id+"F30.wireOp",EDGE,"E101")])],"isStart":false});
            var sketch = newSketch(context, id + "F32", { "sketchPlane" : qUnion([Q0])});
            skPoint(sketch, "E109.0", {"position": v(-953, -109.53) * mm});
            skPoint(sketch, "E110.0", {"position": v(-917, -109.53) * mm});
            skSolve(sketch);
        }
        {
            var Q0;
            Q0=sQuery(id+"F32.wireOp",VERTEX,"E109.0");
            var Q1;
            Q1=sQuery(id+"F32.wireOp",VERTEX,"E110.0");
            var Q2;
            Q2=makeQuery(id+"F31.opExtrude","SWEPT_BODY",BODY,{"disambiguationData":[OSD([sQuery(id+"F30.wireOp",EDGE,"E96.0.1"),sQuery(id+"F30.wireOp",EDGE,"E98"),sQuery(id+"F30.wireOp",EDGE,"E99"),sQuery(id+"F30.wireOp",EDGE,"E100"),sQuery(id+"F30.wireOp",EDGE,"E101")])]});
            hole(context, id + "F33", {"style" : HoleStyle.SIMPLE, "endStyle" : HoleEndStyle.THROUGH, "standardTappedOrClearance" : lookupTablePath({ "standard" : "ISO", "engagement" : "75%", "pitch" : "1.25 mm", "size" : "M8", "type" : "Tapped" }), "standardBlindInLast" : lookupTablePath({ "standard" : "ISO", "engagement" : "75%", "pitch" : "1.25 mm", "size" : "M8", "type" : "Tapped" }), "holeDiameter" : 6.8 * mm, "locations" : qUnion([Q0, Q1]), "scope" : qUnion([Q2]), "isTappedThrough" : true, "majorDiameter" : 8 * mm, "showTappedDepth" : true});
        }
        {
            var Q0;
            Q0=makeQuery(id+"F31.opExtrude","SWEPT_FACE",FACE,{"disambiguationData":[OSD([sQuery(id+"F30.wireOp",EDGE,"E101")])]});
            var sketch = newSketch(context, id + "F34", { "sketchPlane" : qUnion([Q0])});
            skLineSegment(sketch, "E111.0", {"start": v(-35, -81.03) * mm, "end": v(35, -81.03) * mm, "construction": true});
            skLineSegment(sketch, "E112", {"start": v(0, -81.03) * mm, "end": v(0, -181.86) * mm, "construction": true});
            skPoint(sketch, "E112.endSnap0", {"position": v(0, -81.03) * mm});
            skLineSegment(sketch, "E113.0", {"start": v(-15.5, -81.03) * mm, "end": v(-15.5, -181.86) * mm, "construction": true});
            skLineSegment(sketch, "E114", {"start": v(35, -166.03) * mm, "end": v(-35, -166.03) * mm, "construction": true});
            skLineSegment(sketch, "E115.0", {"start": v(35, -148.53) * mm, "end": v(35, -113.53) * mm, "construction": true});
            skLineSegment(sketch, "E116", {"start": v(35, -131.03) * mm, "end": v(-53.23, -131.03) * mm, "construction": true});
            skLineSegment(sketch, "E117.0", {"start": v(35, -87.03) * mm, "end": v(-53.23, -87.03) * mm, "construction": true});
            skLineSegment(sketch, "E118.bottom", {"start": v(-15.5, -166.03) * mm, "end": v(15.5, -166.03) * mm});
            skLineSegment(sketch, "E118.top", {"start": v(-15.5, -87.03) * mm, "end": v(15.5, -87.03) * mm});
            skLineSegment(sketch, "E118.left", {"start": v(-15.5, -166.03) * mm, "end": v(-15.5, -87.03) * mm});
            skLineSegment(sketch, "E118.right", {"start": v(15.5, -166.03) * mm, "end": v(15.5, -87.03) * mm});
            skSolve(sketch);
        }
        {
            var Q0;
            Q0=qSketchRegion(id+"F34",true);
            extrude(context, id + "F35", {"entities" : qUnion([Q0]), "operationType" : NewBodyOperationType.REMOVE, "endBound" : BoundingType.THROUGH_ALL, "oppositeDirection" : true, "depth" : 25 * mm});
        }
        {
            var Q0;
            Q0=makeQuery(id+"F35.boolean.opBoolean","COPY",EDGE,{"derivedFrom":makeQuery(id+"F35.opExtrude","SWEPT_EDGE",EDGE,{"disambiguationData":[OSD([sQuery(id+"F34.wireOp",EDGE,"E118.top"),sQuery(id+"F34.wireOp",EDGE,"E118.right")])]})});
            var Q1;
            Q1=makeQuery(id+"F35.boolean.opBoolean","COPY",EDGE,{"derivedFrom":makeQuery(id+"F35.opExtrude","SWEPT_EDGE",EDGE,{"disambiguationData":[OSD([sQuery(id+"F34.wireOp",EDGE,"E118.top"),sQuery(id+"F34.wireOp",EDGE,"E118.left")])]})});
            fillet(context, id + "F36", {"entities" : qUnion([Q0, Q1]), "radius" : 2 * mm, "tangentPropagation" : true, "allowEdgeOverflow" : false});
        }
        {
            var Q0;
            Q0=makeQuery(id+"F31.opExtrude","SWEPT_BODY",BODY,{"disambiguationData":[OSD([sQuery(id+"F30.wireOp",EDGE,"E96.0.1"),sQuery(id+"F30.wireOp",EDGE,"E98"),sQuery(id+"F30.wireOp",EDGE,"E99"),sQuery(id+"F30.wireOp",EDGE,"E100"),sQuery(id+"F30.wireOp",EDGE,"E101")])]});
            var Q1;
            Q1=qCreatedBy(makeId("Right.planeOp"),FACE);
            mirror(context, id + "F37", {"entities" : qUnion([Q0]), "mirrorPlane" : qUnion([Q1])});
        }
        {
            var Q0;
            Q0=makeQuery(id+"F1.opExtrude","SWEPT_FACE",FACE,{"disambiguationData":[OSD([sQuery(id+"F0.wireOp",EDGE,"E0.bottom")])]});
            var sketch = newSketch(context, id + "F38", { "sketchPlane" : qUnion([Q0])});
            skLineSegment(sketch, "E119", {"start": v(0, 374.52) * mm, "end": v(0, -390.73) * mm, "construction": true});
            skLineSegment(sketch, "E120.0", {"start": v(-880, 374.52) * mm, "end": v(-880, -390.73) * mm, "construction": true});
            skLineSegment(sketch, "E121.0", {"start": v(-925, 374.52) * mm, "end": v(-925, -390.73) * mm, "construction": true});
            skLineSegment(sketch, "E122.0", {"start": v(-874.2, 374.52) * mm, "end": v(-874.2, -390.73) * mm, "construction": true});
            skPoint(sketch, "E123.endSnap0", {"position": v(0, -8.1) * mm});
            skLineSegment(sketch, "E124.0.0", {"start": v(-990, 77.22) * mm, "end": v(-990, -77.22) * mm, "construction": true});
            skLineSegment(sketch, "E124.0.1", {"start": v(-990, -77.22) * mm, "end": v(990, -77.22) * mm, "construction": true});
            skLineSegment(sketch, "E124.0.2", {"start": v(990, -77.22) * mm, "end": v(990, 77.22) * mm, "construction": true});
            skLineSegment(sketch, "E124.0.3", {"start": v(990, 77.22) * mm, "end": v(-990, 77.22) * mm, "construction": true});
            skLineSegment(sketch, "E125", {"start": v(-990, 0) * mm, "end": v(-602.18, 0) * mm, "construction": true});
            skLineSegment(sketch, "E126.0", {"start": v(-990, 60) * mm, "end": v(-602.18, 60) * mm, "construction": true});
            skLineSegment(sketch, "E127.bottom", {"start": v(-925, 60) * mm, "end": v(-874.2, 60) * mm});
            skLineSegment(sketch, "E127.top", {"start": v(-925, -60) * mm, "end": v(-874.2, -60) * mm});
            skLineSegment(sketch, "E127.left", {"start": v(-925, 60) * mm, "end": v(-925, -60) * mm});
            skLineSegment(sketch, "E127.right", {"start": v(-874.2, 60) * mm, "end": v(-874.2, -60) * mm});
            skSolve(sketch);
        }
        {
            var Q0;
            Q0=qSketchRegion(id+"F38",true);
            extrude(context, id + "F39", {"entities" : qUnion([Q0]), "depth" : 120 * mm});
        }
        {
            var Q0;
            Q0=makeQuery(id+"F39.opExtrude","SWEPT_FACE",FACE,{"disambiguationData":[OSD([sQuery(id+"F38.wireOp",EDGE,"E127.left")])]});
            var sketch = newSketch(context, id + "F40", { "sketchPlane" : qUnion([Q0])});
            skLineSegment(sketch, "E128.0", {"start": v(35, -113.53) * mm, "end": v(35, -148.53) * mm, "construction": true});
            skLineSegment(sketch, "E129", {"start": v(35, -131.03) * mm, "end": v(-153.9, -131.03) * mm, "construction": true});
            skLineSegment(sketch, "E130.0", {"start": v(35, 168.97) * mm, "end": v(-153.9, 168.97) * mm, "construction": true});
            skLineSegment(sketch, "E131.0", {"start": v(-60, 201.03) * mm, "end": v(60, 201.03) * mm});
            skLineSegment(sketch, "E132", {"start": v(0, 201.03) * mm, "end": v(0, 143.76) * mm, "construction": true});
            skPoint(sketch, "E132.endSnap0", {"position": v(0, 201.03) * mm});
            skArc(sketch, "E133", {"start": v(-22.5, 168.97) * mm, "mid": v(0, 146.47) * mm, "end": v(22.5, 168.97) * mm});
            skLineSegment(sketch, "E134.0", {"start": v(60, 185.97) * mm, "end": v(22.5, 185.97) * mm});
            skLineSegment(sketch, "E135", {"start": v(-22.5, 168.97) * mm, "end": v(-22.5, 185.97) * mm});
            skLineSegment(sketch, "E136", {"start": v(22.5, 168.97) * mm, "end": v(22.5, 185.97) * mm});
            skLineSegment(sketch, "E137.0", {"start": v(60, 201.03) * mm, "end": v(60, 185.97) * mm});
            skLineSegment(sketch, "E138.0", {"start": v(-60, 201.03) * mm, "end": v(-60, 185.97) * mm});
            skPoint(sketch, "E139.orphan", {"position": v(-60, 81.03) * mm});
            skPoint(sketch, "E140.orphan", {"position": v(60, 81.03) * mm});
            skLineSegment(sketch, "E141.trimOffspring", {"start": v(-22.5, 185.97) * mm, "end": v(-60, 185.97) * mm});
            skSolve(sketch);
        }
        {
            var Q0;
            Q0=qSketchRegion(id+"F40",true);
            extrude(context, id + "F41", {"entities" : qUnion([Q0]), "operationType" : NewBodyOperationType.REMOVE, "endBound" : BoundingType.THROUGH_ALL, "oppositeDirection" : true, "depth" : 25 * mm});
        }
        {
            var Q0;
            Q0=makeQuery(id+"F41.boolean.opBoolean","COPY",FACE,{"derivedFrom":makeQuery(id+"F41.opExtrude","SWEPT_FACE",FACE,{"disambiguationData":[OSD([sQuery(id+"F40.wireOp",EDGE,"E141.trimOffspring")])]})});
            var sketch = newSketch(context, id + "F42", { "sketchPlane" : qUnion([Q0])});
            skLineSegment(sketch, "E142.0", {"start": v(-874.2, 60) * mm, "end": v(-874.2, 22.5) * mm, "construction": true});
            skLineSegment(sketch, "E143.0", {"start": v(-874.2, -60) * mm, "end": v(-925, -60) * mm, "construction": true});
            skLineSegment(sketch, "E144.bottom", {"start": v(-874.2, 60) * mm, "end": v(-880, 60) * mm});
            skLineSegment(sketch, "E144.top", {"start": v(-874.2, -60) * mm, "end": v(-880, -60) * mm});
            skLineSegment(sketch, "E144.left", {"start": v(-874.2, 60) * mm, "end": v(-874.2, -60) * mm});
            skLineSegment(sketch, "E144.right", {"start": v(-880, 60) * mm, "end": v(-880, -60) * mm});
            skLineSegment(sketch, "E145.0", {"start": v(-925, 22.5) * mm, "end": v(-925, 60) * mm, "construction": true});
            skSolve(sketch);
        }
        {
            var Q0;
            Q0=qSketchRegion(id+"F42",true);
            extrude(context, id + "F43", {"entities" : qUnion([Q0]), "operationType" : NewBodyOperationType.REMOVE, "oppositeDirection" : true, "depth" : 92 * mm});
        }
        {
            var Q0;
            Q0=makeQuery(id+"F41.boolean.opBoolean","COPY",FACE,{"derivedFrom":makeQuery(id+"F41.opExtrude","SWEPT_FACE",FACE,{"disambiguationData":[OSD([sQuery(id+"F40.wireOp",EDGE,"E141.trimOffspring")])]})});
            var sketch = newSketch(context, id + "F44", { "sketchPlane" : qUnion([Q0])});
            skLineSegment(sketch, "E146.0.0", {"start": v(-880, 22.5) * mm, "end": v(-880, 60) * mm, "construction": true});
            skLineSegment(sketch, "E146.0.1", {"start": v(-880, 60) * mm, "end": v(-925, 60) * mm, "construction": true});
            skLineSegment(sketch, "E146.0.2", {"start": v(-925, 60) * mm, "end": v(-925, 22.5) * mm, "construction": true});
            skLineSegment(sketch, "E146.0.3", {"start": v(-925, 22.5) * mm, "end": v(-880, 22.5) * mm, "construction": true});
            skLineSegment(sketch, "E147.0.0", {"start": v(-880, -60) * mm, "end": v(-880, -22.5) * mm, "construction": true});
            skLineSegment(sketch, "E147.0.1", {"start": v(-880, -22.5) * mm, "end": v(-925, -22.5) * mm, "construction": true});
            skLineSegment(sketch, "E147.0.2", {"start": v(-925, -22.5) * mm, "end": v(-925, -60) * mm, "construction": true});
            skLineSegment(sketch, "E147.0.3", {"start": v(-925, -60) * mm, "end": v(-880, -60) * mm, "construction": true});
            skLineSegment(sketch, "E148", {"start": v(-902.5, 60) * mm, "end": v(-902.5, -60) * mm, "construction": true});
            skLineSegment(sketch, "E149", {"start": v(-902.5, 0) * mm, "end": v(-937.6, 0) * mm, "construction": true});
            skLineSegment(sketch, "E150.0", {"start": v(-902.5, 37.5) * mm, "end": v(-937.6, 37.5) * mm, "construction": true});
            skPoint(sketch, "E151", {"position": v(-902.5, 37.5) * mm});
            skPoint(sketch, "E152.MirrorP", {"position": v(-902.5, -37.5) * mm});
            skSolve(sketch);
        }
        {
            var Q0;
            Q0=sQuery(id+"F44.wireOp",VERTEX,"E151");
            var Q1;
            Q1=sQuery(id+"F44.wireOp",VERTEX,"E152.MirrorP");
            var Q2;
            Q2=makeQuery(id+"F39.opExtrude","SWEPT_BODY",BODY,{"disambiguationData":[OSD([sQuery(id+"F38.wireOp",EDGE,"E127.bottom"),sQuery(id+"F38.wireOp",EDGE,"E127.top"),sQuery(id+"F38.wireOp",EDGE,"E127.left"),sQuery(id+"F38.wireOp",EDGE,"E127.right")])]});
            hole(context, id + "F45", {"style" : HoleStyle.SIMPLE, "endStyle" : HoleEndStyle.BLIND, "standardTappedOrClearance" : lookupTablePath({ "standard" : "ISO", "engagement" : "75%", "pitch" : "1.25 mm", "size" : "M12", "type" : "Tapped" }), "standardBlindInLast" : lookupTablePath({ "standard" : "ISO", "engagement" : "75%", "pitch" : "1.25 mm", "size" : "M12", "type" : "Tapped" }), "holeDiameter" : 10.8 * mm, "holeDepth" : 35 * mm, "locations" : qUnion([Q0, Q1]), "scope" : qUnion([Q2]), "majorDiameter" : 12 * mm});
        }
        {
            var Q0;
            Q0=makeQuery(id+"F39.opExtrude","SWEPT_BODY",BODY,{"disambiguationData":[OSD([sQuery(id+"F38.wireOp",EDGE,"E127.bottom"),sQuery(id+"F38.wireOp",EDGE,"E127.top"),sQuery(id+"F38.wireOp",EDGE,"E127.left"),sQuery(id+"F38.wireOp",EDGE,"E127.right")])]});
            var Q1;
            Q1=qCreatedBy(makeId("Right.planeOp"),FACE);
            mirror(context, id + "F46", {"entities" : qUnion([Q0]), "mirrorPlane" : qUnion([Q1])});
        }
        {
            var Q0;
            Q0=qCreatedBy(makeId("Right.planeOp"),FACE);
            cPlane(context, id + "F47", {"entities" : qUnion([Q0]), "cplaneType" : CPlaneType.OFFSET, "offset" : (330 / 2 + 15) * mm, "width" : 150 * mm, "height" : 150 * mm});
        }
        {
            var Q0;
            Q0=qCreatedBy(id+"F47.planeOp",FACE);
            var sketch = newSketch(context, id + "F48", { "sketchPlane" : qUnion([Q0])});
            skLineSegment(sketch, "E153", {"start": v(0, 256.72) * mm, "end": v(0, -431.7) * mm, "construction": true});
            skLineSegment(sketch, "E154.0.0", {"start": v(-60, 81.03) * mm, "end": v(-60, 185.97) * mm, "construction": true});
            skLineSegment(sketch, "E154.0.1", {"start": v(-60, 185.97) * mm, "end": v(-22.5, 185.97) * mm, "construction": true});
            skLineSegment(sketch, "E154.0.2", {"start": v(-22.5, 185.97) * mm, "end": v(-22.5, 168.97) * mm, "construction": true});
            skArc(sketch, "E154.0.3", {"start": v(-22.5, 168.97) * mm, "mid": v(0, 146.47) * mm, "end": v(22.5, 168.97) * mm, "construction": true});
            skLineSegment(sketch, "E154.0.4", {"start": v(22.5, 168.97) * mm, "end": v(22.5, 185.97) * mm, "construction": true});
            skLineSegment(sketch, "E154.0.5", {"start": v(22.5, 185.97) * mm, "end": v(144, 185.97) * mm, "construction": true});
            skLineSegment(sketch, "E154.0.6", {"start": v(60, 185.97) * mm, "end": v(60, 81.03) * mm, "construction": true});
            skLineSegment(sketch, "E154.0.7", {"start": v(60, 81.03) * mm, "end": v(-60, 81.03) * mm, "construction": true});
            skLineSegment(sketch, "E155.0", {"start": v(144, 256.72) * mm, "end": v(144, -69.47) * mm});
            skLineSegment(sketch, "E156.0.0", {"start": v(77.22, 81.03) * mm, "end": v(77.22, 69.47) * mm, "construction": true});
            skLineSegment(sketch, "E156.0.1", {"start": v(77.22, 69.47) * mm, "end": v(-77.22, 69.47) * mm, "construction": true});
            skLineSegment(sketch, "E156.0.2", {"start": v(-77.22, 69.47) * mm, "end": v(-77.22, 81.03) * mm, "construction": true});
            skLineSegment(sketch, "E156.0.3", {"start": v(-77.22, 81.03) * mm, "end": v(77.22, 81.03) * mm, "construction": true});
            skLineSegment(sketch, "E157.0.0", {"start": v(-77.22, -69.47) * mm, "end": v(144, -69.47) * mm, "construction": true});
            skLineSegment(sketch, "E157.0.1", {"start": v(77.22, -69.47) * mm, "end": v(77.22, -81.03) * mm, "construction": true});
            skLineSegment(sketch, "E157.0.2", {"start": v(77.22, -81.03) * mm, "end": v(-77.22, -81.03) * mm, "construction": true});
            skLineSegment(sketch, "E157.0.3", {"start": v(-77.22, -81.03) * mm, "end": v(-77.22, -69.47) * mm, "construction": true});
            skLineSegment(sketch, "E158.0.0", {"start": v(16.76, -69.47) * mm, "end": v(-16.76, -69.47) * mm, "construction": true});
            skArc(sketch, "E158.0.1", {"start": v(-16.76, -69.47) * mm, "mid": v(-7.78, -65.75) * mm, "end": v(-4.06, -56.77) * mm, "construction": true});
            skLineSegment(sketch, "E158.0.2", {"start": v(-4.06, -56.77) * mm, "end": v(-4.06, 56.77) * mm, "construction": true});
            skArc(sketch, "E158.0.3", {"start": v(-4.06, 56.77) * mm, "mid": v(-7.78, 65.75) * mm, "end": v(-16.76, 69.47) * mm, "construction": true});
            skLineSegment(sketch, "E158.0.4", {"start": v(-16.76, 69.47) * mm, "end": v(16.76, 69.47) * mm, "construction": true});
            skArc(sketch, "E158.0.5", {"start": v(16.76, 69.47) * mm, "mid": v(7.78, 65.75) * mm, "end": v(4.06, 56.77) * mm, "construction": true});
            skLineSegment(sketch, "E158.0.6", {"start": v(4.06, 56.77) * mm, "end": v(4.06, -56.77) * mm, "construction": true});
            skArc(sketch, "E158.0.7", {"start": v(4.06, -56.77) * mm, "mid": v(7.78, -65.75) * mm, "end": v(16.76, -69.47) * mm, "construction": true});
            skLineSegment(sketch, "E159", {"start": v(144, 185.97) * mm, "end": v(77.22, 197.75) * mm});
            skLineSegment(sketch, "E160.0", {"start": v(70, 86.03) * mm, "end": v(77.22, 86.03) * mm, "construction": true});
            skLineSegment(sketch, "E161.0", {"start": v(77.22, 199.02) * mm, "end": v(77.22, 69.47) * mm});
            skLineSegment(sketch, "E162", {"start": v(144, 30.53) * mm, "end": v(80.74, -69.47) * mm});
            skLineSegment(sketch, "E163", {"start": v(80.74, -69.47) * mm, "end": v(16.76, -69.47) * mm});
            skLineSegment(sketch, "E164", {"start": v(16.76, -69.47) * mm, "end": v(4.06, -56.77) * mm});
            skLineSegment(sketch, "E165", {"start": v(4.06, -56.77) * mm, "end": v(4.06, 56.77) * mm});
            skLineSegment(sketch, "E166", {"start": v(4.06, 56.77) * mm, "end": v(16.76, 69.47) * mm});
            skLineSegment(sketch, "E167", {"start": v(16.76, 69.47) * mm, "end": v(77.22, 69.47) * mm});
            skLineSegment(sketch, "E168", {"start": v(77.22, 69.47) * mm, "end": v(77.22, 86.03) * mm});
            skLineSegment(sketch, "E169", {"start": v(77.22, 86.03) * mm, "end": v(70, 86.03) * mm});
            skLineSegment(sketch, "E170", {"start": v(70, 185.97) * mm, "end": v(70, 199.02) * mm});
            skLineSegment(sketch, "E171", {"start": v(144, 185.97) * mm, "end": v(144, 30.53) * mm});
            skLineSegment(sketch, "E172", {"start": v(77.22, 199.02) * mm, "end": v(91.33, 199.02) * mm});
            skLineSegment(sketch, "E173", {"start": v(77.22, 199.02) * mm, "end": v(150.28, 186.14) * mm});
            skSolve(sketch);
        }
        {
            var Q0;
            Q0=qSketchRegion(id+"F48",true);
            extrude(context, id + "F49", {"entities" : qUnion([Q0]), "oppositeDirection" : true, "depth" : 15.88 * mm});
        }
        {
            var Q0;
            Q0=makeQuery(id+"F49.opExtrude","CAP_FACE",FACE,{"disambiguationData":[OSD([sQuery(id+"F48.wireOp",EDGE,"E159"),sQuery(id+"F48.wireOp",EDGE,"E162"),sQuery(id+"F48.wireOp",EDGE,"E163"),sQuery(id+"F48.wireOp",EDGE,"E164"),sQuery(id+"F48.wireOp",EDGE,"E165"),sQuery(id+"F48.wireOp",EDGE,"E166"),sQuery(id+"F48.wireOp",EDGE,"E167"),sQuery(id+"F48.wireOp",EDGE,"E168"),sQuery(id+"F48.wireOp",EDGE,"E169"),sQuery(id+"F48.wireOp",EDGE,"E170"),sQuery(id+"F48.wireOp",EDGE,"E171")])],"isStart":true});
            var sketch = newSketch(context, id + "F50", { "sketchPlane" : qUnion([Q0])});
            skLineSegment(sketch, "E174.0.4", {"start": v(80.74, -69.47) * mm, "end": v(144, 30.53) * mm});
            skLineSegment(sketch, "E174.0.5", {"start": v(16.76, -69.47) * mm, "end": v(80.74, -69.47) * mm});
            skLineSegment(sketch, "E174.0.6", {"start": v(4.06, -56.77) * mm, "end": v(16.76, -69.47) * mm});
            skLineSegment(sketch, "E174.0.7", {"start": v(4.06, 56.77) * mm, "end": v(4.06, -56.77) * mm});
            skLineSegment(sketch, "E174.0.8", {"start": v(16.76, 69.47) * mm, "end": v(4.06, 56.77) * mm});
            skLineSegment(sketch, "E174.0.9", {"start": v(77.22, 69.47) * mm, "end": v(16.76, 69.47) * mm});
            skLineSegment(sketch, "E174.0.10", {"start": v(77.22, 86.03) * mm, "end": v(77.22, 69.47) * mm});
            skLineSegment(sketch, "E175.0.0", {"start": v(144, 187.25) * mm, "end": v(77.22, 199.02) * mm});
            skLineSegment(sketch, "E175.0.1", {"start": v(77.22, 199.02) * mm, "end": v(77.22, 137.25) * mm});
            skLineSegment(sketch, "E175.0.8", {"start": v(144, 137.25) * mm, "end": v(144, 187.25) * mm});
            skLineSegment(sketch, "E176", {"start": v(77.22, 137.25) * mm, "end": v(144, 137.25) * mm});
            skSolve(sketch);
        }
        {
            var Q0;
            Q0=qSketchRegion(id+"F50",true);
            extrude(context, id + "F51", {"entities" : qUnion([Q0]), "depth" : 19 * mm});
        }
        {
            var Q0;
            Q0=makeQuery(id+"F51.opExtrude","SWEPT_FACE",FACE,{"disambiguationData":[OSD([sQuery(id+"F50.wireOp",EDGE,"E175.0.0")])]});
            var sketch = newSketch(context, id + "F52", { "sketchPlane" : qUnion([Q0])});
            skLineSegment(sketch, "E177", {"start": v(0, 185.79) * mm, "end": v(0, -149.3) * mm, "construction": true});
            skLineSegment(sketch, "E178.0", {"start": v(190, 185.79) * mm, "end": v(190, -149.3) * mm, "construction": true});
            skLineSegment(sketch, "E179.0.0", {"start": v(180, 109.52) * mm, "end": v(180, 34.38) * mm, "construction": true});
            skLineSegment(sketch, "E179.0.1", {"start": v(180, 34.38) * mm, "end": v(205.4, 34.38) * mm, "construction": true});
            skLineSegment(sketch, "E179.0.2", {"start": v(205.4, 34.38) * mm, "end": v(205.4, 109.52) * mm, "construction": true});
            skLineSegment(sketch, "E179.0.3", {"start": v(205.4, 109.52) * mm, "end": v(180, 109.52) * mm, "construction": true});
            skLineSegment(sketch, "E180.0", {"start": v(205.4, 69.52) * mm, "end": v(180, 69.52) * mm, "construction": true});
            skLineSegment(sketch, "E181.0", {"start": v(205.4, 94.52) * mm, "end": v(180, 94.52) * mm, "construction": true});
            skPoint(sketch, "E182", {"position": v(190, 94.52) * mm});
            skPoint(sketch, "E183", {"position": v(190, 69.52) * mm});
            skSolve(sketch);
        }
        {
            var Q0;
            Q0=sQuery(id+"F52.wireOp",VERTEX,"E182");
            var Q1;
            Q1=sQuery(id+"F52.wireOp",VERTEX,"E183");
            var Q2;
            Q2=makeQuery(id+"F51.opExtrude","SWEPT_BODY",BODY,{"disambiguationData":[OSD([sQuery(id+"F50.wireOp",EDGE,"E175.0.0"),sQuery(id+"F50.wireOp",EDGE,"E175.0.1"),sQuery(id+"F50.wireOp",EDGE,"E175.0.8"),sQuery(id+"F50.wireOp",EDGE,"E176")])]});
            hole(context, id + "F53", {"style" : HoleStyle.SIMPLE, "endStyle" : HoleEndStyle.BLIND, "standardTappedOrClearance" : lookupTablePath({ "standard" : "ISO", "engagement" : "75%", "pitch" : "1.5 mm", "size" : "M12", "type" : "Tapped" }), "standardBlindInLast" : lookupTablePath({ "standard" : "ISO", "engagement" : "75%", "pitch" : "1.5 mm", "size" : "M12", "type" : "Tapped" }), "holeDiameter" : 10.5 * mm, "holeDepth" : 30 * mm, "locations" : qUnion([Q0, Q1]), "scope" : qUnion([Q2]), "majorDiameter" : 12 * mm});
        }
        {
            var Q0;
            Q0=makeQuery(id+"F49.opExtrude","SWEPT_BODY",BODY,{"disambiguationData":[OSD([sQuery(id+"F48.wireOp",EDGE,"E159"),sQuery(id+"F48.wireOp",EDGE,"E162"),sQuery(id+"F48.wireOp",EDGE,"E163"),sQuery(id+"F48.wireOp",EDGE,"E164"),sQuery(id+"F48.wireOp",EDGE,"E165"),sQuery(id+"F48.wireOp",EDGE,"E166"),sQuery(id+"F48.wireOp",EDGE,"E167"),sQuery(id+"F48.wireOp",EDGE,"E168"),sQuery(id+"F48.wireOp",EDGE,"E169"),sQuery(id+"F48.wireOp",EDGE,"E170"),sQuery(id+"F48.wireOp",EDGE,"E171")])]});
            var Q1;
            Q1=makeQuery(id+"Fl3NnRKCw4Xixsh_5.opExtrude","SWEPT_BODY",BODY,{"disambiguationData":[OSD([sQuery(id+"F50.wireOp",EDGE,"E174.0.2"),sQuery(id+"F50.wireOp",EDGE,"L5QzTxGx-Pnf6-FATO-cNnD-iBCD0eLFIrfw"),sQuery(id+"F50.wireOp",EDGE,"wuJ0hKJl-j7K5-ufxr-qZVR-Fc0DleJu5Dkg"),sQuery(id+"F50.wireOp",EDGE,"Ftl8TeeW-pfTl-imrB-EIy6-TxBNQzbVambr")])]});
            var Q2;
            Q2=qCreatedBy(makeId("Right.planeOp"),FACE);
            mirror(context, id + "F54", {"entities" : qUnion([Q0, Q1]), "mirrorPlane" : qUnion([Q2])});
        }
        {
            var Q0;
            Q0=qCreatedBy(id+"F47.planeOp",FACE);
            cPlane(context, id + "F55", {"entities" : qUnion([Q0]), "cplaneType" : CPlaneType.OFFSET, "offset" : 350 * mm, "width" : 150 * mm, "height" : 150 * mm});
        }
        {
            var Q0;
            Q0=makeQuery(id+"F49.opExtrude","SWEPT_BODY",BODY,{"disambiguationData":[OSD([sQuery(id+"F48.wireOp",EDGE,"E159"),sQuery(id+"F48.wireOp",EDGE,"E162"),sQuery(id+"F48.wireOp",EDGE,"E163"),sQuery(id+"F48.wireOp",EDGE,"E164"),sQuery(id+"F48.wireOp",EDGE,"E165"),sQuery(id+"F48.wireOp",EDGE,"E166"),sQuery(id+"F48.wireOp",EDGE,"E167"),sQuery(id+"F48.wireOp",EDGE,"E168"),sQuery(id+"F48.wireOp",EDGE,"E169"),sQuery(id+"F48.wireOp",EDGE,"E170"),sQuery(id+"F48.wireOp",EDGE,"E171")])]});
            var Q1;
            Q1=makeQuery(id+"Fl3NnRKCw4Xixsh_5.opExtrude","SWEPT_BODY",BODY,{"disambiguationData":[OSD([sQuery(id+"F50.wireOp",EDGE,"E174.0.2"),sQuery(id+"F50.wireOp",EDGE,"L5QzTxGx-Pnf6-FATO-cNnD-iBCD0eLFIrfw"),sQuery(id+"F50.wireOp",EDGE,"wuJ0hKJl-j7K5-ufxr-qZVR-Fc0DleJu5Dkg"),sQuery(id+"F50.wireOp",EDGE,"Ftl8TeeW-pfTl-imrB-EIy6-TxBNQzbVambr")])]});
            var Q2;
            Q2=qCreatedBy(id+"F55.planeOp",FACE);
            mirror(context, id + "F56", {"entities" : qUnion([Q0, Q1]), "mirrorPlane" : qUnion([Q2])});
        }
        {
            var Q0;
            Q0=makeQuery(id+"F56.opPattern","COPY",BODY,{"derivedFrom":makeQuery(id+"F49.opExtrude","SWEPT_BODY",BODY,{"disambiguationData":[OSD([sQuery(id+"F48.wireOp",EDGE,"E159"),sQuery(id+"F48.wireOp",EDGE,"E162"),sQuery(id+"F48.wireOp",EDGE,"E163"),sQuery(id+"F48.wireOp",EDGE,"E164"),sQuery(id+"F48.wireOp",EDGE,"E165"),sQuery(id+"F48.wireOp",EDGE,"E166"),sQuery(id+"F48.wireOp",EDGE,"E167"),sQuery(id+"F48.wireOp",EDGE,"E168"),sQuery(id+"F48.wireOp",EDGE,"E169"),sQuery(id+"F48.wireOp",EDGE,"E170"),sQuery(id+"F48.wireOp",EDGE,"E171")])]}),"instanceName":"1"});
            var Q1;
            Q1=makeQuery(id+"F56.opPattern","COPY",BODY,{"derivedFrom":makeQuery(id+"Fl3NnRKCw4Xixsh_5.opExtrude","SWEPT_BODY",BODY,{"disambiguationData":[OSD([sQuery(id+"F50.wireOp",EDGE,"E174.0.2"),sQuery(id+"F50.wireOp",EDGE,"L5QzTxGx-Pnf6-FATO-cNnD-iBCD0eLFIrfw"),sQuery(id+"F50.wireOp",EDGE,"wuJ0hKJl-j7K5-ufxr-qZVR-Fc0DleJu5Dkg"),sQuery(id+"F50.wireOp",EDGE,"Ftl8TeeW-pfTl-imrB-EIy6-TxBNQzbVambr")])]}),"instanceName":"1"});
            var Q2;
            Q2=qCreatedBy(makeId("Right.planeOp"),FACE);
            mirror(context, id + "F57", {"entities" : qUnion([Q0, Q1]), "mirrorPlane" : qUnion([Q2])});
        }
        {
            var Q0;
            Q0=qCreatedBy(id+"F47.planeOp",FACE);
            var sketch = newSketch(context, id + "F58", { "sketchPlane" : qUnion([Q0])});
            skLineSegment(sketch, "E184", {"start": v(0, 263.92) * mm, "end": v(0, -250.39) * mm, "construction": true});
            skLineSegment(sketch, "E185.0", {"start": v(-206, 263.92) * mm, "end": v(-206, -250.39) * mm, "construction": true});
            skLineSegment(sketch, "E186.0.0", {"start": v(77.22, 81.03) * mm, "end": v(77.22, 69.47) * mm, "construction": true});
            skLineSegment(sketch, "E186.0.1", {"start": v(77.22, 69.47) * mm, "end": v(-77.22, 69.47) * mm, "construction": true});
            skLineSegment(sketch, "E186.0.2", {"start": v(-77.22, 69.47) * mm, "end": v(-77.22, 81.03) * mm, "construction": true});
            skLineSegment(sketch, "E186.0.3", {"start": v(-77.22, 81.03) * mm, "end": v(77.22, 81.03) * mm, "construction": true});
            skLineSegment(sketch, "E187.0.0", {"start": v(16.76, -69.47) * mm, "end": v(-16.76, -69.47) * mm, "construction": true});
            skArc(sketch, "E187.0.1", {"start": v(-16.76, -69.47) * mm, "mid": v(-7.78, -65.75) * mm, "end": v(-4.06, -56.77) * mm, "construction": true});
            skLineSegment(sketch, "E187.0.2", {"start": v(-4.06, -56.77) * mm, "end": v(-4.06, 56.77) * mm, "construction": true});
            skArc(sketch, "E187.0.3", {"start": v(-4.06, 56.77) * mm, "mid": v(-7.78, 65.75) * mm, "end": v(-16.76, 69.47) * mm, "construction": true});
            skLineSegment(sketch, "E187.0.4", {"start": v(-16.76, 69.47) * mm, "end": v(16.76, 69.47) * mm, "construction": true});
            skArc(sketch, "E187.0.5", {"start": v(16.76, 69.47) * mm, "mid": v(7.78, 65.75) * mm, "end": v(4.06, 56.77) * mm, "construction": true});
            skLineSegment(sketch, "E187.0.6", {"start": v(4.06, 56.77) * mm, "end": v(4.06, -56.77) * mm, "construction": true});
            skArc(sketch, "E187.0.7", {"start": v(4.06, -56.77) * mm, "mid": v(7.78, -65.75) * mm, "end": v(16.76, -69.47) * mm, "construction": true});
            skLineSegment(sketch, "E188.0.0", {"start": v(-77.22, -69.47) * mm, "end": v(77.22, -69.47) * mm, "construction": true});
            skLineSegment(sketch, "E188.0.1", {"start": v(77.22, -69.47) * mm, "end": v(77.22, -81.03) * mm, "construction": true});
            skLineSegment(sketch, "E188.0.2", {"start": v(77.22, -81.03) * mm, "end": v(-77.22, -81.03) * mm, "construction": true});
            skLineSegment(sketch, "E188.0.3", {"start": v(-77.22, -81.03) * mm, "end": v(-77.22, -69.47) * mm, "construction": true});
            skLineSegment(sketch, "E189.0", {"start": v(-206, 10.53) * mm, "end": v(77.22, 10.53) * mm, "construction": true});
            skLineSegment(sketch, "E190", {"start": v(-77.22, 69.47) * mm, "end": v(-16.76, 69.47) * mm});
            skLineSegment(sketch, "E191", {"start": v(-16.76, 69.47) * mm, "end": v(-4.06, 56.77) * mm});
            skLineSegment(sketch, "E192", {"start": v(-4.06, 56.77) * mm, "end": v(-4.06, -56.77) * mm});
            skLineSegment(sketch, "E193", {"start": v(-16.76, -69.47) * mm, "end": v(-4.06, -56.77) * mm});
            skLineSegment(sketch, "E194", {"start": v(-16.76, -69.47) * mm, "end": v(-77.22, -69.47) * mm});
            skLineSegment(sketch, "E195", {"start": v(-77.22, -69.47) * mm, "end": v(-206, 10.53) * mm});
            skLineSegment(sketch, "E196", {"start": v(-77.22, 69.47) * mm, "end": v(-77.22, 185.97) * mm});
            skLineSegment(sketch, "E197.0.0", {"start": v(-60, 81.03) * mm, "end": v(-60, 185.97) * mm});
            skLineSegment(sketch, "E197.0.1", {"start": v(-60, 185.97) * mm, "end": v(-22.5, 185.97) * mm});
            skLineSegment(sketch, "E197.0.2", {"start": v(-22.5, 185.97) * mm, "end": v(-22.5, 168.97) * mm});
            skArc(sketch, "E197.0.3", {"start": v(-22.5, 168.97) * mm, "mid": v(0, 146.47) * mm, "end": v(22.5, 168.97) * mm});
            skLineSegment(sketch, "E197.0.4", {"start": v(22.5, 168.97) * mm, "end": v(22.5, 185.97) * mm});
            skLineSegment(sketch, "E197.0.7", {"start": v(60, 81.03) * mm, "end": v(-60, 81.03) * mm});
            skPoint(sketch, "E197.0.6.start.orphan", {"position": v(60, 185.97) * mm});
            skLineSegment(sketch, "E198", {"start": v(-77.22, 185.97) * mm, "end": v(-222.54, 185.97) * mm, "construction": true});
            skLineSegment(sketch, "E199", {"start": v(-77.22, 185.97) * mm, "end": v(-206, 111.62) * mm});
            skLineSegment(sketch, "E200", {"start": v(-206, 111.62) * mm, "end": v(-206, 10.53) * mm});
            skSolve(sketch);
        }
        {
            var Q0;
            Q0=qSketchRegion(id+"F58",true);
            extrude(context, id + "F59", {"entities" : qUnion([Q0]), "oppositeDirection" : true, "depth" : 16 * mm});
        }
        {
            var Q0;
            Q0=makeQuery(id+"F59.opExtrude","CAP_FACE",FACE,{"disambiguationData":[OSD([sQuery(id+"F58.wireOp",EDGE,"E190"),sQuery(id+"F58.wireOp",EDGE,"E191"),sQuery(id+"F58.wireOp",EDGE,"E192"),sQuery(id+"F58.wireOp",EDGE,"E193"),sQuery(id+"F58.wireOp",EDGE,"E194"),sQuery(id+"F58.wireOp",EDGE,"E195"),sQuery(id+"F58.wireOp",EDGE,"E196"),sQuery(id+"F58.wireOp",EDGE,"E199"),sQuery(id+"F58.wireOp",EDGE,"E200")])],"isStart":false});
            var sketch = newSketch(context, id + "F60", { "sketchPlane" : qUnion([Q0])});
            skLineSegment(sketch, "E201.0.0", {"start": v(206, 111.62) * mm, "end": v(77.22, 185.97) * mm, "construction": true});
            skLineSegment(sketch, "E201.0.1", {"start": v(77.22, 185.97) * mm, "end": v(77.22, 69.47) * mm, "construction": true});
            skLineSegment(sketch, "E201.0.2", {"start": v(77.22, 69.47) * mm, "end": v(16.76, 69.47) * mm, "construction": true});
            skLineSegment(sketch, "E201.0.3", {"start": v(16.76, 69.47) * mm, "end": v(4.06, 56.77) * mm, "construction": true});
            skLineSegment(sketch, "E201.0.4", {"start": v(4.06, 56.77) * mm, "end": v(4.06, -56.77) * mm, "construction": true});
            skLineSegment(sketch, "E201.0.5", {"start": v(4.06, -56.77) * mm, "end": v(16.76, -69.47) * mm, "construction": true});
            skLineSegment(sketch, "E201.0.6", {"start": v(16.76, -69.47) * mm, "end": v(77.22, -69.47) * mm, "construction": true});
            skLineSegment(sketch, "E201.0.7", {"start": v(77.22, -69.47) * mm, "end": v(206, 10.53) * mm, "construction": true});
            skLineSegment(sketch, "E201.0.8", {"start": v(206, 10.53) * mm, "end": v(206, 111.62) * mm, "construction": true});
            skLineSegment(sketch, "E202.0", {"start": v(191, 85.64) * mm, "end": v(62.22, 160) * mm, "construction": true});
            skLineSegment(sketch, "E203", {"start": v(191, 85.64) * mm, "end": v(206, 111.62) * mm, "construction": true});
            skLineSegment(sketch, "E204.0", {"start": v(178, 93.14) * mm, "end": v(193, 119.12) * mm, "construction": true});
            skLineSegment(sketch, "E205.0", {"start": v(100.07, 138.14) * mm, "end": v(115.07, 164.12) * mm, "construction": true});
            skPoint(sketch, "E206", {"position": v(100.07, 138.14) * mm});
            skPoint(sketch, "E207", {"position": v(178, 93.14) * mm});
            skSolve(sketch);
        }
        {
            var Q0;
            Q0=sQuery(id+"F60.wireOp",VERTEX,"E206");
            var Q1;
            Q1=sQuery(id+"F60.wireOp",VERTEX,"E207");
            var Q2;
            Q2=makeQuery(id+"F59.opExtrude","SWEPT_BODY",BODY,{"disambiguationData":[OSD([sQuery(id+"F58.wireOp",EDGE,"E190"),sQuery(id+"F58.wireOp",EDGE,"E191"),sQuery(id+"F58.wireOp",EDGE,"E192"),sQuery(id+"F58.wireOp",EDGE,"E193"),sQuery(id+"F58.wireOp",EDGE,"E194"),sQuery(id+"F58.wireOp",EDGE,"E195"),sQuery(id+"F58.wireOp",EDGE,"E196"),sQuery(id+"F58.wireOp",EDGE,"E199"),sQuery(id+"F58.wireOp",EDGE,"E200")])]});
            hole(context, id + "F61", {"style" : HoleStyle.SIMPLE, "endStyle" : HoleEndStyle.BLIND, "standardTappedOrClearance" : lookupTablePath({ "standard" : "ISO", "size" : "12", "type" : "Drilled" }), "standardBlindInLast" : lookupTablePath({ "standard" : "ISO", "size" : "12", "type" : "Drilled" }), "holeDiameter" : 12 * mm, "holeDepth" : 30 * mm, "locations" : qUnion([Q0, Q1]), "scope" : qUnion([Q2])});
        }
        {
            var Q0;
            Q0=makeQuery(id+"F59.opExtrude","SWEPT_BODY",BODY,{"disambiguationData":[OSD([sQuery(id+"F58.wireOp",EDGE,"E190"),sQuery(id+"F58.wireOp",EDGE,"E191"),sQuery(id+"F58.wireOp",EDGE,"E192"),sQuery(id+"F58.wireOp",EDGE,"E193"),sQuery(id+"F58.wireOp",EDGE,"E194"),sQuery(id+"F58.wireOp",EDGE,"E195"),sQuery(id+"F58.wireOp",EDGE,"E196"),sQuery(id+"F58.wireOp",EDGE,"E199"),sQuery(id+"F58.wireOp",EDGE,"E200")])]});
            var Q1;
            Q1=qCreatedBy(makeId("Right.planeOp"),FACE);
            mirror(context, id + "F62", {"entities" : qUnion([Q0]), "mirrorPlane" : qUnion([Q1])});
        }
        {
            var Q0;
            Q0=makeQuery(id+"F59.opExtrude","SWEPT_BODY",BODY,{"disambiguationData":[OSD([sQuery(id+"F58.wireOp",EDGE,"E190"),sQuery(id+"F58.wireOp",EDGE,"E191"),sQuery(id+"F58.wireOp",EDGE,"E192"),sQuery(id+"F58.wireOp",EDGE,"E193"),sQuery(id+"F58.wireOp",EDGE,"E194"),sQuery(id+"F58.wireOp",EDGE,"E195"),sQuery(id+"F58.wireOp",EDGE,"E196"),sQuery(id+"F58.wireOp",EDGE,"E199"),sQuery(id+"F58.wireOp",EDGE,"E200")])]});
            var Q1;
            Q1=qCreatedBy(id+"F55.planeOp",FACE);
            mirror(context, id + "F63", {"entities" : qUnion([Q0]), "mirrorPlane" : qUnion([Q1])});
        }
        {
            var Q0;
            Q0=makeQuery(id+"F63.opPattern","COPY",BODY,{"derivedFrom":makeQuery(id+"F59.opExtrude","SWEPT_BODY",BODY,{"disambiguationData":[OSD([sQuery(id+"F58.wireOp",EDGE,"E190"),sQuery(id+"F58.wireOp",EDGE,"E191"),sQuery(id+"F58.wireOp",EDGE,"E192"),sQuery(id+"F58.wireOp",EDGE,"E193"),sQuery(id+"F58.wireOp",EDGE,"E194"),sQuery(id+"F58.wireOp",EDGE,"E195"),sQuery(id+"F58.wireOp",EDGE,"E196"),sQuery(id+"F58.wireOp",EDGE,"E199"),sQuery(id+"F58.wireOp",EDGE,"E200")])]}),"instanceName":"1"});
            var Q1;
            Q1=qCreatedBy(makeId("Right.planeOp"),FACE);
            mirror(context, id + "F64", {"operationType" : NewBodyOperationType.ADD, "entities" : qUnion([Q0]), "mirrorPlane" : qUnion([Q1])});
        }
        {
            var Q0;
            Q0=makeQuery(id+"F5.opExtrude","SWEPT_EDGE",EDGE,{"disambiguationData":[OSD([sQuery(id+"F4.wireOp",EDGE,"E50.bottom"),sQuery(id+"F4.wireOp",EDGE,"E50.right")])]});
            var Q1;
            Q1=makeQuery(id+"F5.opExtrude","SWEPT_EDGE",EDGE,{"disambiguationData":[OSD([sQuery(id+"F4.wireOp",EDGE,"E50.top"),sQuery(id+"F4.wireOp",EDGE,"E52.trimOffspring")])]});
            chamfer(context, id + "F65", {"entities" : qUnion([Q0, Q1]), "width" : 5 * mm, "tangentPropagation" : true});
        }
        {
            var Q0;
            Q0=makeQuery(id+"F29.opPattern","COPY",EDGE,{"derivedFrom":makeQuery(id+"F5.opExtrude","SWEPT_EDGE",EDGE,{"disambiguationData":[OSD([sQuery(id+"F4.wireOp",EDGE,"E50.bottom"),sQuery(id+"F4.wireOp",EDGE,"E50.right")])]}),"instanceName":"1"});
            var Q1;
            Q1=makeQuery(id+"F29.opPattern","COPY",EDGE,{"derivedFrom":makeQuery(id+"F5.opExtrude","SWEPT_EDGE",EDGE,{"disambiguationData":[OSD([sQuery(id+"F4.wireOp",EDGE,"E50.top"),sQuery(id+"F4.wireOp",EDGE,"E52.trimOffspring")])]}),"instanceName":"1"});
            chamfer(context, id + "F66", {"entities" : qUnion([Q0, Q1]), "width" : 5 * mm, "tangentPropagation" : true});
        }
        {
            var Q0;
            Q0=makeQuery(id+"F63.opPattern","COPY",FACE,{"derivedFrom":makeQuery(id+"F59.opExtrude","CAP_FACE",FACE,{"disambiguationData":[OSD([sQuery(id+"F58.wireOp",EDGE,"E190"),sQuery(id+"F58.wireOp",EDGE,"E191"),sQuery(id+"F58.wireOp",EDGE,"E192"),sQuery(id+"F58.wireOp",EDGE,"E193"),sQuery(id+"F58.wireOp",EDGE,"E194"),sQuery(id+"F58.wireOp",EDGE,"E195"),sQuery(id+"F58.wireOp",EDGE,"E196"),sQuery(id+"F58.wireOp",EDGE,"E199"),sQuery(id+"F58.wireOp",EDGE,"E200")])],"isStart":false}),"instanceName":"1"});
            var sketch = newSketch(context, id + "F67", { "sketchPlane" : qUnion([Q0])});
            skLineSegment(sketch, "E208.0", {"start": v(-35, -113.53) * mm, "end": v(-35, -148.53) * mm, "construction": true});
            skLineSegment(sketch, "E209", {"start": v(-35, -131.03) * mm, "end": v(-367.6, -131.03) * mm, "construction": true});
            skLineSegment(sketch, "E210.0", {"start": v(-35, -16.03) * mm, "end": v(-367.6, -16.03) * mm, "construction": true});
            skLineSegment(sketch, "E211.0", {"start": v(-35, 23.97) * mm, "end": v(-367.6, 23.97) * mm, "construction": true});
            skLineSegment(sketch, "E212", {"start": v(0, 332.63) * mm, "end": v(0, -263.23) * mm, "construction": true});
            skLineSegment(sketch, "E213.0", {"start": v(-140, 23.97) * mm, "end": v(-140, -16.03) * mm, "construction": true});
            skLineSegment(sketch, "E214.trimOffspring", {"start": v(-140, -131.03) * mm, "end": v(-140, -263.23) * mm, "construction": true});
            skLineSegment(sketch, "E215.bottom", {"start": v(-160, 23.97) * mm, "end": v(-120, 23.97) * mm});
            skLineSegment(sketch, "E215.top", {"start": v(-160, -16.03) * mm, "end": v(-120, -16.03) * mm});
            skLineSegment(sketch, "E215.left", {"start": v(-160, 23.97) * mm, "end": v(-160, -16.03) * mm});
            skLineSegment(sketch, "E215.right", {"start": v(-120, 23.97) * mm, "end": v(-120, -16.03) * mm});
            skPoint(sketch, "E215.middle", {"position": v(-140, 3.97) * mm});
            skSolve(sketch);
        }
        {
            var Q0;
            Q0=qSketchRegion(id+"F67",true);
            extrude(context, id + "F68", {"entities" : qUnion([Q0]), "depth" : 60 * mm});
        }
        {
            var Q0;
            Q0=makeQuery(id+"F68.opExtrude","SWEPT_FACE",FACE,{"disambiguationData":[OSD([sQuery(id+"F67.wireOp",EDGE,"E215.bottom")])]});
            var sketch = newSketch(context, id + "F69", { "sketchPlane" : qUnion([Q0])});
            skLineSegment(sketch, "E216.0", {"start": v(917.5, -35) * mm, "end": v(952.5, -35) * mm, "construction": true});
            skLineSegment(sketch, "E217", {"start": v(935, -120) * mm, "end": v(935, -160) * mm, "construction": true});
            skLineSegment(sketch, "E218.0.0", {"start": v(896, -120) * mm, "end": v(896, -160) * mm, "construction": true});
            skLineSegment(sketch, "E218.0.1", {"start": v(896, -160) * mm, "end": v(956, -160) * mm, "construction": true});
            skLineSegment(sketch, "E218.0.2", {"start": v(956, -160) * mm, "end": v(956, -120) * mm, "construction": true});
            skLineSegment(sketch, "E218.0.3", {"start": v(956, -120) * mm, "end": v(896, -120) * mm, "construction": true});
            skLineSegment(sketch, "E219", {"start": v(956, -140) * mm, "end": v(857.2, -140) * mm, "construction": true});
            skPoint(sketch, "E219.endSnap0", {"position": v(956, -140) * mm});
            skPoint(sketch, "E220.orphan", {"position": v(935, -35) * mm});
            skPoint(sketch, "E221", {"position": v(935, -140) * mm});
            skSolve(sketch);
        }
        {
            var Q0;
            Q0=sQuery(id+"F69.wireOp",VERTEX,"E221");
            var Q1;
            Q1=makeQuery(id+"F68.opExtrude","SWEPT_BODY",BODY,{"disambiguationData":[OSD([sQuery(id+"F67.wireOp",EDGE,"E215.bottom"),sQuery(id+"F67.wireOp",EDGE,"E215.top"),sQuery(id+"F67.wireOp",EDGE,"E215.left"),sQuery(id+"F67.wireOp",EDGE,"E215.right")])]});
            hole(context, id + "F70", {"style" : HoleStyle.SIMPLE, "endStyle" : HoleEndStyle.THROUGH, "standardTappedOrClearance" : lookupTablePath({ "standard" : "ISO", "size" : "20", "type" : "Drilled" }), "standardBlindInLast" : lookupTablePath({ "standard" : "ISO", "size" : "20", "type" : "Drilled" }), "holeDiameter" : 20 * mm, "locations" : qUnion([Q0]), "scope" : qUnion([Q1]), "isTappedThrough" : true});
        }
        {
            var Q0;
            Q0=makeQuery(id+"F68.opExtrude","SWEPT_FACE",FACE,{"disambiguationData":[OSD([sQuery(id+"F67.wireOp",EDGE,"E215.left")])]});
            var sketch = newSketch(context, id + "F71", { "sketchPlane" : qUnion([Q0])});
            skLineSegment(sketch, "E222.0", {"start": v(925, 23.97) * mm, "end": v(945, 23.97) * mm, "construction": true});
            skLineSegment(sketch, "E223", {"start": v(935, 23.97) * mm, "end": v(935, -16.03) * mm, "construction": true});
            skLineSegment(sketch, "E224.0", {"start": v(956, -16.03) * mm, "end": v(896, -16.03) * mm, "construction": true});
            skPoint(sketch, "E225", {"position": v(935, 3.97) * mm});
            skSolve(sketch);
        }
        {
            var Q0;
            Q0=sQuery(id+"F71.wireOp",VERTEX,"E225");
            var Q1;
            Q1=makeQuery(id+"F68.opExtrude","SWEPT_BODY",BODY,{"disambiguationData":[OSD([sQuery(id+"F67.wireOp",EDGE,"E215.bottom"),sQuery(id+"F67.wireOp",EDGE,"E215.top"),sQuery(id+"F67.wireOp",EDGE,"E215.left"),sQuery(id+"F67.wireOp",EDGE,"E215.right")])]});
            hole(context, id + "F72", {"style" : HoleStyle.SIMPLE, "endStyle" : HoleEndStyle.THROUGH, "standardTappedOrClearance" : lookupTablePath({ "standard" : "ISO", "size" : "8", "type" : "Drilled" }), "standardBlindInLast" : lookupTablePath({ "standard" : "ISO", "size" : "8", "type" : "Drilled" }), "holeDiameter" : 8 * mm, "locations" : qUnion([Q0]), "scope" : qUnion([Q1]), "isTappedThrough" : true});
        }
        {
            var Q0;
            Q0=makeQuery(id+"F68.opExtrude","SWEPT_BODY",BODY,{"disambiguationData":[OSD([sQuery(id+"F67.wireOp",EDGE,"E215.bottom"),sQuery(id+"F67.wireOp",EDGE,"E215.top"),sQuery(id+"F67.wireOp",EDGE,"E215.left"),sQuery(id+"F67.wireOp",EDGE,"E215.right")])]});
            var Q1;
            Q1=qCreatedBy(makeId("Right.planeOp"),FACE);
            mirror(context, id + "F73", {"entities" : qUnion([Q0]), "mirrorPlane" : qUnion([Q1])});
        }
        {
            var Q0;
            Q0=makeQuery(id+"F51.opExtrude","SWEPT_BODY",BODY,{"disambiguationData":[OSD([sQuery(id+"F50.wireOp",EDGE,"E175.0.0"),sQuery(id+"F50.wireOp",EDGE,"E175.0.1"),sQuery(id+"F50.wireOp",EDGE,"E175.0.8"),sQuery(id+"F50.wireOp",EDGE,"E176")])]});
            var Q1;
            Q1=qCreatedBy(id+"F55.planeOp",FACE);
            mirror(context, id + "F74", {"entities" : qUnion([Q0]), "mirrorPlane" : qUnion([Q1])});
        }
        {
            var Q0;
            Q0=makeQuery(id+"F51.opExtrude","SWEPT_BODY",BODY,{"disambiguationData":[OSD([sQuery(id+"F50.wireOp",EDGE,"E175.0.0"),sQuery(id+"F50.wireOp",EDGE,"E175.0.1"),sQuery(id+"F50.wireOp",EDGE,"E175.0.8"),sQuery(id+"F50.wireOp",EDGE,"E176")])]});
            var Q1;
            Q1=makeQuery(id+"F74.opPattern","COPY",BODY,{"derivedFrom":makeQuery(id+"F51.opExtrude","SWEPT_BODY",BODY,{"disambiguationData":[OSD([sQuery(id+"F50.wireOp",EDGE,"E175.0.0"),sQuery(id+"F50.wireOp",EDGE,"E175.0.1"),sQuery(id+"F50.wireOp",EDGE,"E175.0.8"),sQuery(id+"F50.wireOp",EDGE,"E176")])]}),"instanceName":"1"});
            var Q2;
            Q2=qCreatedBy(makeId("Right.planeOp"),FACE);
            mirror(context, id + "F75", {"entities" : qUnion([Q0, Q1]), "mirrorPlane" : qUnion([Q2])});
        }
        {
            var Q0;
            Q0=makeQuery(id+"F1.opExtrude","SWEPT_BODY",BODY,{"disambiguationData":[OSD([sQuery(id+"F0.wireOp",EDGE,"E0.bottom"),sQuery(id+"F0.wireOp",EDGE,"E0.top"),sQuery(id+"F0.wireOp",EDGE,"E0.left"),sQuery(id+"F0.wireOp",EDGE,"E0.right"),sQuery(id+"F0.wireOp",EDGE,"E2.0"),sQuery(id+"F0.wireOp",EDGE,"E3.0"),sQuery(id+"F0.wireOp",EDGE,"E4.0"),sQuery(id+"F0.wireOp",EDGE,"E5.0"),sQuery(id+"F0.wireOp",EDGE,"E6.trimOffspring"),sQuery(id+"F0.wireOp",EDGE,"E7.trimOffspring"),sQuery(id+"F0.wireOp",EDGE,"E8.trimOffspring"),sQuery(id+"F0.wireOp",EDGE,"E9.trimOffspring"),sQuery(id+"F0.wireOp",EDGE,"E10.filletArc"),sQuery(id+"F0.wireOp",EDGE,"E11.filletArc"),sQuery(id+"F0.wireOp",EDGE,"E12.filletArc"),sQuery(id+"F0.wireOp",EDGE,"E13.filletArc")])]});
            var Q1;
            Q1=makeQuery(id+"F62.opPattern","COPY",BODY,{"derivedFrom":makeQuery(id+"F59.opExtrude","SWEPT_BODY",BODY,{"disambiguationData":[OSD([sQuery(id+"F58.wireOp",EDGE,"E190"),sQuery(id+"F58.wireOp",EDGE,"E191"),sQuery(id+"F58.wireOp",EDGE,"E192"),sQuery(id+"F58.wireOp",EDGE,"E193"),sQuery(id+"F58.wireOp",EDGE,"E194"),sQuery(id+"F58.wireOp",EDGE,"E195"),sQuery(id+"F58.wireOp",EDGE,"E196"),sQuery(id+"F58.wireOp",EDGE,"E199"),sQuery(id+"F58.wireOp",EDGE,"E200")])]}),"instanceName":"1"});
            var Q2;
            Q2=makeQuery(id+"F59.opExtrude","SWEPT_BODY",BODY,{"disambiguationData":[OSD([sQuery(id+"F58.wireOp",EDGE,"E190"),sQuery(id+"F58.wireOp",EDGE,"E191"),sQuery(id+"F58.wireOp",EDGE,"E192"),sQuery(id+"F58.wireOp",EDGE,"E193"),sQuery(id+"F58.wireOp",EDGE,"E194"),sQuery(id+"F58.wireOp",EDGE,"E195"),sQuery(id+"F58.wireOp",EDGE,"E196"),sQuery(id+"F58.wireOp",EDGE,"E199"),sQuery(id+"F58.wireOp",EDGE,"E200")])]});
            booleanBodies(context, id + "F76", {"operationType" : BooleanOperationType.UNION, "tools" : qUnion([Q0, Q1, Q2])});
        }
        {
            var Q0;
            Q0=makeQuery(id+"F1.opExtrude","SWEPT_FACE",FACE,{"disambiguationData":[OSD([sQuery(id+"F0.wireOp",EDGE,"E8.trimOffspring")])]});
            var sketch = newSketch(context, id + "F77", { "sketchPlane" : qUnion([Q0])});
            skLineSegment(sketch, "E226.0", {"start": v(990, -81.03) * mm, "end": v(-990, -81.03) * mm, "construction": true});
            skLineSegment(sketch, "E227", {"start": v(0, 255.13) * mm, "end": v(0, -180.02) * mm, "construction": true});
            skLineSegment(sketch, "E228.0", {"start": v(990, 18.97) * mm, "end": v(-990, 18.97) * mm, "construction": true});
            skLineSegment(sketch, "E229.0", {"start": v(1002.25, -56.03) * mm, "end": v(-990, -56.03) * mm, "construction": true});
            skArc(sketch, "E230", {"start": v(81.12, -56.03) * mm, "mid": v(6.12, 18.97) * mm, "end": v(-68.88, -56.03) * mm});
            skLineSegment(sketch, "E231", {"start": v(-68.88, -56.03) * mm, "end": v(-68.87, -81.03) * mm});
            skLineSegment(sketch, "E232", {"start": v(81.12, -56.03) * mm, "end": v(81.12, -81.03) * mm});
            skLineSegment(sketch, "E233.0", {"start": v(-80, -56.03) * mm, "end": v(-80, -81.03) * mm});
            skArc(sketch, "E233.1", {"start": v(92.25, -56.03) * mm, "mid": v(6.13, 30.1) * mm, "end": v(-80, -56.03) * mm});
            skLineSegment(sketch, "E233.2", {"start": v(92.25, -56.03) * mm, "end": v(92.25, -81.03) * mm});
            skLineSegment(sketch, "E234", {"start": v(-80, -81.03) * mm, "end": v(-68.87, -81.03) * mm});
            skLineSegment(sketch, "E235", {"start": v(81.12, -81.03) * mm, "end": v(92.25, -81.03) * mm});
            skSolve(sketch);
        }
        {
            var Q0;
            Q0=qSketchRegion(id+"F77",true);
            var Q1;
            Q1=makeQuery(id+"F1.opExtrude","SWEPT_FACE",FACE,{"disambiguationData":[OSD([sQuery(id+"F0.wireOp",EDGE,"E9.trimOffspring")])]});
            extrude(context, id + "F78", {"entities" : qUnion([Q0]), "operationType" : NewBodyOperationType.ADD, "endBound" : BoundingType.UP_TO_SURFACE, "oppositeDirection" : true, "endBoundEntityFace" : qUnion([Q1]), "depth" : 25 * mm});
        }
        {
            var Q0;
            Q0=makeQuery(id+"F78.boolean.opBoolean","MERGE",FACE,{"derivedFrom":[makeQuery(id+"F1.opExtrude","SWEPT_FACE",FACE,{"disambiguationData":[OSD([sQuery(id+"F0.wireOp",EDGE,"E8.trimOffspring")])]}),makeQuery(id+"F78.opExtrude","CAP_FACE",FACE,{"disambiguationData":[OSD([sQuery(id+"F77.wireOp",EDGE,"E230"),sQuery(id+"F77.wireOp",EDGE,"E231"),sQuery(id+"F77.wireOp",EDGE,"E232"),sQuery(id+"F77.wireOp",EDGE,"E233.0"),sQuery(id+"F77.wireOp",EDGE,"E233.1"),sQuery(id+"F77.wireOp",EDGE,"E233.2"),sQuery(id+"F77.wireOp",EDGE,"E234"),sQuery(id+"F77.wireOp",EDGE,"E235")])],"isStart":true})]});
            var sketch = newSketch(context, id + "F79", { "sketchPlane" : qUnion([Q0])});
            skArc(sketch, "E236.0", {"start": v(81.12, -56.03) * mm, "mid": v(6.12, 18.97) * mm, "end": v(-68.88, -56.03) * mm});
            skLineSegment(sketch, "E237.0", {"start": v(-68.88, -56.03) * mm, "end": v(-68.87, -81.03) * mm});
            skLineSegment(sketch, "E238.0", {"start": v(81.12, -56.03) * mm, "end": v(81.12, -81.03) * mm});
            skLineSegment(sketch, "E239.0", {"start": v(81.12, -81.03) * mm, "end": v(-68.88, -81.03) * mm});
            skPoint(sketch, "E240.orphan", {"position": v(81.12, -69.47) * mm});
            skPoint(sketch, "E241.orphan", {"position": v(-68.87, -69.47) * mm});
            skPoint(sketch, "E242.orphan", {"position": v(990, -81.03) * mm});
            skPoint(sketch, "E243.orphan", {"position": v(-990, -81.03) * mm});
            skSolve(sketch);
        }
        {
            var Q0;
            Q0=qSketchRegion(id+"F79",true);
            var Q1;
            {var subQ0=sQuery(id+"F0.wireOp",EDGE,"E9.trimOffspring");Q1=makeQuery(id+"F78.boolean.opBoolean","MERGE",FACE,{"derivedFrom":[makeQuery(id+"F1.opExtrude","SWEPT_FACE",FACE,{"disambiguationData":[OSD([subQ0])]}),makeQuery(id+"F78.opExtrude","CAP_FACE",FACE,{"disambiguationData":[OSD([subQ0])],"isStart":false})]});}
            extrude(context, id + "F80", {"entities" : qUnion([Q0]), "operationType" : NewBodyOperationType.REMOVE, "endBound" : BoundingType.UP_TO_SURFACE, "oppositeDirection" : true, "endBoundEntityFace" : qUnion([Q1]), "depth" : 25 * mm});
        }
        {
            var Q0;
            Q0=makeQuery(id+"F78.boolean.opBoolean","MERGE",FACE,{"derivedFrom":[makeQuery(id+"F1.opExtrude","SWEPT_FACE",FACE,{"disambiguationData":[OSD([sQuery(id+"F0.wireOp",EDGE,"E8.trimOffspring")])]}),makeQuery(id+"F78.opExtrude","CAP_FACE",FACE,{"disambiguationData":[OSD([sQuery(id+"F77.wireOp",EDGE,"E230"),sQuery(id+"F77.wireOp",EDGE,"E231"),sQuery(id+"F77.wireOp",EDGE,"E232"),sQuery(id+"F77.wireOp",EDGE,"E233.0"),sQuery(id+"F77.wireOp",EDGE,"E233.1"),sQuery(id+"F77.wireOp",EDGE,"E233.2"),sQuery(id+"F77.wireOp",EDGE,"E234"),sQuery(id+"F77.wireOp",EDGE,"E235")])],"isStart":true})]});
            var sketch = newSketch(context, id + "F81", { "sketchPlane" : qUnion([Q0])});
            skLineSegment(sketch, "E244.0.0", {"start": v(81.12, -56.03) * mm, "end": v(81.12, -81.03) * mm});
            skLineSegment(sketch, "E244.0.1", {"start": v(81.12, -81.03) * mm, "end": v(92.25, -81.03) * mm});
            skLineSegment(sketch, "E244.0.2", {"start": v(990, -81.03) * mm, "end": v(990, -69.47) * mm});
            skLineSegment(sketch, "E244.0.3", {"start": v(990, -69.47) * mm, "end": v(896, -69.47) * mm});
            skLineSegment(sketch, "E244.0.4", {"start": v(896, -69.47) * mm, "end": v(880, -69.47) * mm});
            skLineSegment(sketch, "E244.0.5", {"start": v(880, -69.47) * mm, "end": v(180, -69.47) * mm});
            skLineSegment(sketch, "E244.0.6", {"start": v(180, -69.47) * mm, "end": v(164, -69.47) * mm});
            skLineSegment(sketch, "E244.0.8", {"start": v(92.25, -81.03) * mm, "end": v(92.25, -56.03) * mm});
            skArc(sketch, "E244.0.9", {"start": v(92.25, -56.03) * mm, "mid": v(6.13, 30.1) * mm, "end": v(-80, -56.03) * mm});
            skLineSegment(sketch, "E244.0.10", {"start": v(-80, -56.03) * mm, "end": v(-80, -81.03) * mm});
            skLineSegment(sketch, "E244.0.12", {"start": v(-164, -69.47) * mm, "end": v(-180, -69.47) * mm});
            skLineSegment(sketch, "E244.0.13", {"start": v(-180, -69.47) * mm, "end": v(-880, -69.47) * mm});
            skLineSegment(sketch, "E244.0.14", {"start": v(-880, -69.47) * mm, "end": v(-896, -69.47) * mm});
            skLineSegment(sketch, "E244.0.15", {"start": v(-896, -69.47) * mm, "end": v(-990, -69.47) * mm});
            skLineSegment(sketch, "E244.0.16", {"start": v(-990, -69.47) * mm, "end": v(-990, -81.03) * mm});
            skLineSegment(sketch, "E244.0.17", {"start": v(-80, -81.03) * mm, "end": v(-68.88, -81.03) * mm});
            skLineSegment(sketch, "E244.0.18", {"start": v(-68.87, -81.03) * mm, "end": v(-68.88, -56.03) * mm});
            skArc(sketch, "E244.0.19", {"start": v(-68.88, -56.03) * mm, "mid": v(6.12, 18.97) * mm, "end": v(81.12, -56.03) * mm});
            skPoint(sketch, "E244.0.11.start.orphan", {"position": v(-80, -69.47) * mm});
            skPoint(sketch, "E244.0.7.end.orphan", {"position": v(92.25, -69.47) * mm});
            skSolve(sketch);
        }
        {
            var Q0;
            Q0 = qSketchRegion(id + "F81", true);
            extrude(context, id + "F82", {"entities" : qUnion([Q0]), "operationType" : NewBodyOperationType.REMOVE, "endBound" : BoundingType.THROUGH_ALL, "oppositeDirection" : true, "depth" : 25 * mm});
        }
    });
